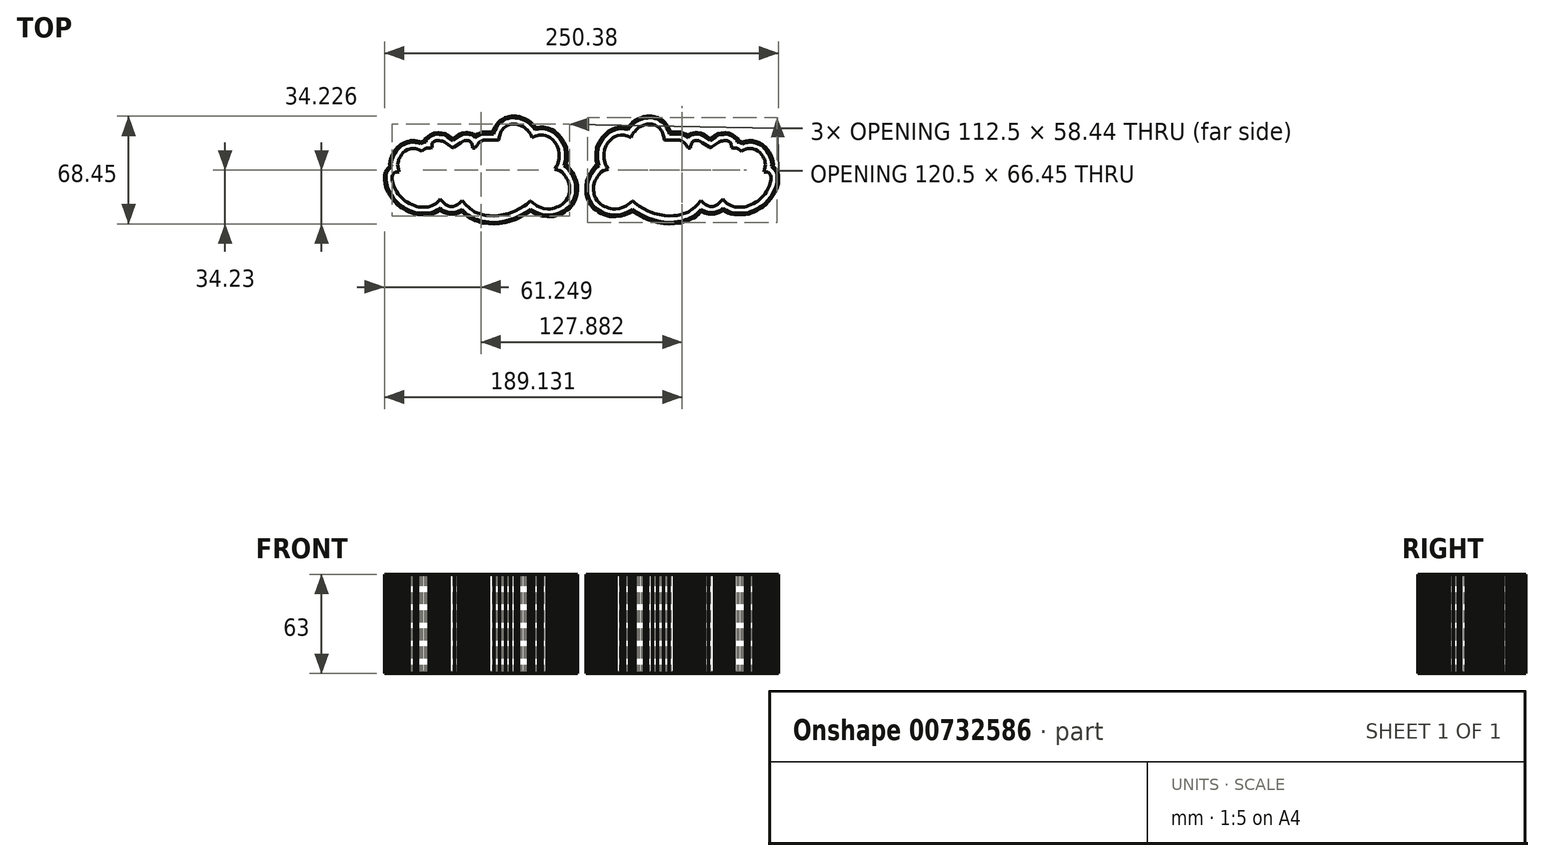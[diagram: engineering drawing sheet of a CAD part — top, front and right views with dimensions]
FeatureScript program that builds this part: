
annotation { "Feature Type Name" : "Feature", "Feature Type Description" : "" }
export const myFeature = defineFeature(function(context is Context, id is Id, definition is map)
    precondition{}
    {
        {
            var Q0;
            Q0=qCreatedBy(makeId("Top.planeOp"),FACE);
            var sketch = newSketch(context, id + "F0", { "sketchPlane" : qUnion([Q0])});
            skLineSegment(sketch, "E0", {"start": v(-23.19, 24.45) * mm, "end": v(-22.89, 24.98) * mm});
            skLineSegment(sketch, "E1", {"start": v(-22.89, 24.98) * mm, "end": v(-22.45, 25.83) * mm});
            skLineSegment(sketch, "E2", {"start": v(-22.45, 25.83) * mm, "end": v(-21.79, 26.88) * mm});
            skLineSegment(sketch, "E3", {"start": v(-21.79, 26.88) * mm, "end": v(-21.29, 27.75) * mm});
            skLineSegment(sketch, "E4", {"start": v(-21.29, 27.75) * mm, "end": v(-20.65, 28.52) * mm});
            skLineSegment(sketch, "E5", {"start": v(-20.65, 28.52) * mm, "end": v(-20.04, 29.22) * mm});
            skLineSegment(sketch, "E6", {"start": v(-20.04, 29.22) * mm, "end": v(-19.69, 29.6) * mm});
            skLineSegment(sketch, "E7", {"start": v(-19.69, 29.6) * mm, "end": v(-18.9, 30.34) * mm});
            skLineSegment(sketch, "E8", {"start": v(-18.9, 30.34) * mm, "end": v(-18.23, 30.85) * mm});
            skLineSegment(sketch, "E9", {"start": v(-18.23, 30.85) * mm, "end": v(-17.55, 31.28) * mm});
            skLineSegment(sketch, "E10", {"start": v(-17.55, 31.28) * mm, "end": v(-16.9, 31.62) * mm});
            skLineSegment(sketch, "E11", {"start": v(-16.9, 31.62) * mm, "end": v(-16.2, 31.87) * mm});
            skLineSegment(sketch, "E12", {"start": v(-16.2, 31.87) * mm, "end": v(-15.4, 32.17) * mm});
            skLineSegment(sketch, "E13", {"start": v(-15.4, 32.17) * mm, "end": v(-14.74, 32.39) * mm});
            skLineSegment(sketch, "E14", {"start": v(-14.74, 32.39) * mm, "end": v(-13.84, 32.5) * mm});
            skLineSegment(sketch, "E15", {"start": v(-13.84, 32.5) * mm, "end": v(-13.21, 32.57) * mm});
            skLineSegment(sketch, "E16", {"start": v(-13.21, 32.57) * mm, "end": v(-12.54, 32.64) * mm});
            skLineSegment(sketch, "E17", {"start": v(-12.54, 32.64) * mm, "end": v(-11.86, 32.64) * mm});
            skLineSegment(sketch, "E18", {"start": v(-11.86, 32.64) * mm, "end": v(-11.38, 32.52) * mm});
            skLineSegment(sketch, "E19", {"start": v(-11.38, 32.52) * mm, "end": v(-10.33, 32.21) * mm});
            skLineSegment(sketch, "E20", {"start": v(-10.33, 32.21) * mm, "end": v(-9.48, 32.02) * mm});
            skLineSegment(sketch, "E21", {"start": v(-9.48, 32.02) * mm, "end": v(-8.66, 31.5) * mm});
            skLineSegment(sketch, "E22", {"start": v(-8.66, 31.5) * mm, "end": v(-7.93, 31.02) * mm});
            skLineSegment(sketch, "E23", {"start": v(-7.93, 31.02) * mm, "end": v(-7.3, 30.45) * mm});
            skLineSegment(sketch, "E24", {"start": v(-7.3, 30.45) * mm, "end": v(-6.7, 29.75) * mm});
            skLineSegment(sketch, "E25", {"start": v(-6.7, 29.75) * mm, "end": v(-6.2, 29.04) * mm});
            skLineSegment(sketch, "E26", {"start": v(-6.2, 29.04) * mm, "end": v(-5.63, 27.97) * mm});
            skLineSegment(sketch, "E27", {"start": v(-5.63, 27.97) * mm, "end": v(-5.27, 26.99) * mm});
            skLineSegment(sketch, "E28", {"start": v(-5.27, 26.99) * mm, "end": v(-4.96, 25.96) * mm});
            skLineSegment(sketch, "E29", {"start": v(-4.96, 25.96) * mm, "end": v(-4.72, 25.15) * mm});
            skLineSegment(sketch, "E30", {"start": v(-4.72, 25.15) * mm, "end": v(-4.6, 24.61) * mm});
            skLineSegment(sketch, "E31", {"start": v(-4.6, 24.61) * mm, "end": v(-4.6, 23.66) * mm});
            skLineSegment(sketch, "E32", {"start": v(-4.6, 23.66) * mm, "end": v(-4.46, 23.42) * mm});
            skLineSegment(sketch, "E33", {"start": v(-4.46, 23.42) * mm, "end": v(-4.1, 23.02) * mm});
            skLineSegment(sketch, "E34", {"start": v(-4.1, 23.02) * mm, "end": v(-3.67, 22.68) * mm});
            skLineSegment(sketch, "E35", {"start": v(-3.67, 22.68) * mm, "end": v(-3.29, 22.5) * mm});
            skLineSegment(sketch, "E36", {"start": v(-3.29, 22.5) * mm, "end": v(-2.73, 22.4) * mm});
            skLineSegment(sketch, "E37", {"start": v(-2.73, 22.4) * mm, "end": v(-2.06, 22.4) * mm});
            skLineSegment(sketch, "E38", {"start": v(-2.06, 22.4) * mm, "end": v(6.4, 22.4) * mm});
            skLineSegment(sketch, "E39", {"start": v(6.4, 22.4) * mm, "end": v(6.78, 22.31) * mm});
            skLineSegment(sketch, "E40", {"start": v(6.78, 22.31) * mm, "end": v(7.37, 22.04) * mm});
            skLineSegment(sketch, "E41", {"start": v(7.37, 22.04) * mm, "end": v(8.12, 21.59) * mm});
            skLineSegment(sketch, "E42", {"start": v(8.12, 21.59) * mm, "end": v(8.57, 21.14) * mm});
            skLineSegment(sketch, "E43", {"start": v(8.57, 21.14) * mm, "end": v(9.34, 20.19) * mm});
            skLineSegment(sketch, "E44", {"start": v(9.34, 20.19) * mm, "end": v(9.63, 19.65) * mm});
            skLineSegment(sketch, "E45", {"start": v(9.63, 19.65) * mm, "end": v(10.05, 19.02) * mm});
            skLineSegment(sketch, "E46", {"start": v(10.05, 19.02) * mm, "end": v(10.48, 18.48) * mm});
            skLineSegment(sketch, "E47", {"start": v(10.48, 18.48) * mm, "end": v(10.93, 18.03) * mm});
            skLineSegment(sketch, "E48", {"start": v(10.93, 18.03) * mm, "end": v(11.34, 17.7) * mm});
            skLineSegment(sketch, "E49", {"start": v(11.34, 17.7) * mm, "end": v(11.6, 17.57) * mm});
            skLineSegment(sketch, "E50", {"start": v(11.6, 17.57) * mm, "end": v(11.99, 17.4) * mm});
            skLineSegment(sketch, "E51", {"start": v(11.99, 17.4) * mm, "end": v(13.78, 17.4) * mm});
            skLineSegment(sketch, "E52", {"start": v(13.78, 17.4) * mm, "end": v(14.24, 17.4) * mm});
            skLineSegment(sketch, "E53", {"start": v(14.24, 17.4) * mm, "end": v(14.42, 17.52) * mm});
            skLineSegment(sketch, "E54", {"start": v(14.42, 17.52) * mm, "end": v(14.71, 17.67) * mm});
            skLineSegment(sketch, "E55", {"start": v(14.71, 17.67) * mm, "end": v(14.85, 17.98) * mm});
            skLineSegment(sketch, "E56", {"start": v(14.85, 17.98) * mm, "end": v(14.98, 18.27) * mm});
            skLineSegment(sketch, "E57", {"start": v(14.98, 18.27) * mm, "end": v(15.1, 19.02) * mm});
            skLineSegment(sketch, "E58", {"start": v(15.1, 19.02) * mm, "end": v(15.19, 19.75) * mm});
            skLineSegment(sketch, "E59", {"start": v(15.19, 19.75) * mm, "end": v(15.37, 20.46) * mm});
            skLineSegment(sketch, "E60", {"start": v(15.37, 20.46) * mm, "end": v(15.51, 21.04) * mm});
            skLineSegment(sketch, "E61", {"start": v(15.51, 21.04) * mm, "end": v(15.68, 21.4) * mm});
            skLineSegment(sketch, "E62", {"start": v(15.68, 21.4) * mm, "end": v(15.93, 21.76) * mm});
            skLineSegment(sketch, "E63", {"start": v(15.93, 21.76) * mm, "end": v(16.28, 22.04) * mm});
            skLineSegment(sketch, "E64", {"start": v(16.28, 22.04) * mm, "end": v(16.59, 22.12) * mm});
            skLineSegment(sketch, "E65", {"start": v(16.59, 22.12) * mm, "end": v(17.21, 22.22) * mm});
            skLineSegment(sketch, "E66", {"start": v(17.21, 22.22) * mm, "end": v(17.73, 22.22) * mm});
            skLineSegment(sketch, "E67", {"start": v(17.73, 22.22) * mm, "end": v(18.51, 22.12) * mm});
            skLineSegment(sketch, "E68", {"start": v(18.51, 22.12) * mm, "end": v(19.1, 21.85) * mm});
            skLineSegment(sketch, "E69", {"start": v(19.1, 21.85) * mm, "end": v(20, 21.13) * mm});
            skLineSegment(sketch, "E70", {"start": v(20, 21.13) * mm, "end": v(24.79, 18.05) * mm});
            skLineSegment(sketch, "E71", {"start": v(24.79, 18.05) * mm, "end": v(25.26, 17.84) * mm});
            skLineSegment(sketch, "E72", {"start": v(25.26, 17.84) * mm, "end": v(25.52, 17.8) * mm});
            skLineSegment(sketch, "E73", {"start": v(25.52, 17.8) * mm, "end": v(26.08, 17.74) * mm});
            skLineSegment(sketch, "E74", {"start": v(26.08, 17.74) * mm, "end": v(26.62, 17.74) * mm});
            skLineSegment(sketch, "E75", {"start": v(26.62, 17.74) * mm, "end": v(27.51, 18.05) * mm});
            skLineSegment(sketch, "E76", {"start": v(27.51, 18.05) * mm, "end": v(32.34, 21.27) * mm});
            skLineSegment(sketch, "E77", {"start": v(32.34, 21.27) * mm, "end": v(33.33, 21.8) * mm});
            skLineSegment(sketch, "E78", {"start": v(33.33, 21.8) * mm, "end": v(34, 21.95) * mm});
            skLineSegment(sketch, "E79", {"start": v(34, 21.95) * mm, "end": v(35.03, 22.04) * mm});
            skLineSegment(sketch, "E80", {"start": v(35.03, 22.04) * mm, "end": v(35.66, 22.12) * mm});
            skLineSegment(sketch, "E81", {"start": v(35.66, 22.12) * mm, "end": v(36.26, 22.04) * mm});
            skLineSegment(sketch, "E82", {"start": v(36.26, 22.04) * mm, "end": v(37.14, 21.64) * mm});
            skLineSegment(sketch, "E83", {"start": v(37.14, 21.64) * mm, "end": v(37.79, 21.13) * mm});
            skLineSegment(sketch, "E84", {"start": v(37.79, 21.13) * mm, "end": v(37.86, 20.36) * mm});
            skLineSegment(sketch, "E85", {"start": v(37.86, 20.36) * mm, "end": v(37.93, 19.65) * mm});
            skLineSegment(sketch, "E86", {"start": v(37.93, 19.65) * mm, "end": v(38.02, 18.69) * mm});
            skLineSegment(sketch, "E87", {"start": v(38.02, 18.69) * mm, "end": v(38.44, 18.05) * mm});
            skLineSegment(sketch, "E88", {"start": v(38.44, 18.05) * mm, "end": v(38.7, 17.66) * mm});
            skLineSegment(sketch, "E89", {"start": v(38.7, 17.66) * mm, "end": v(39.43, 17.57) * mm});
            skLineSegment(sketch, "E90", {"start": v(39.43, 17.57) * mm, "end": v(40.57, 17.48) * mm});
            skLineSegment(sketch, "E91", {"start": v(40.57, 17.48) * mm, "end": v(41.83, 17.4) * mm});
            skLineSegment(sketch, "E92", {"start": v(41.83, 17.4) * mm, "end": v(42.56, 17.27) * mm});
            skLineSegment(sketch, "E93", {"start": v(42.56, 17.27) * mm, "end": v(43.28, 17) * mm});
            skLineSegment(sketch, "E94", {"start": v(43.28, 17) * mm, "end": v(44.02, 16.5) * mm});
            skLineSegment(sketch, "E95", {"start": v(44.02, 16.5) * mm, "end": v(44.44, 16.08) * mm});
            skLineSegment(sketch, "E96", {"start": v(44.44, 16.08) * mm, "end": v(44.78, 15.66) * mm});
            skLineSegment(sketch, "E97", {"start": v(44.78, 15.66) * mm, "end": v(45.06, 15.27) * mm});
            skLineSegment(sketch, "E98", {"start": v(45.06, 15.27) * mm, "end": v(45.22, 15.07) * mm});
            skLineSegment(sketch, "E99", {"start": v(45.22, 15.07) * mm, "end": v(45.45, 14.99) * mm});
            skLineSegment(sketch, "E100", {"start": v(45.45, 14.99) * mm, "end": v(45.83, 14.99) * mm});
            skLineSegment(sketch, "E101", {"start": v(45.83, 14.99) * mm, "end": v(46.12, 15.18) * mm});
            skLineSegment(sketch, "E102", {"start": v(46.12, 15.18) * mm, "end": v(46.84, 15.62) * mm});
            skLineSegment(sketch, "E103", {"start": v(46.84, 15.62) * mm, "end": v(47.97, 16.16) * mm});
            skLineSegment(sketch, "E104", {"start": v(47.97, 16.16) * mm, "end": v(49.46, 16.7) * mm});
            skLineSegment(sketch, "E105", {"start": v(49.46, 16.7) * mm, "end": v(50.25, 16.93) * mm});
            skLineSegment(sketch, "E106", {"start": v(50.25, 16.93) * mm, "end": v(50.8, 17.04) * mm});
            skLineSegment(sketch, "E107", {"start": v(52.56, 17.04) * mm, "end": v(53.3, 16.85) * mm});
            skLineSegment(sketch, "E108", {"start": v(52.56, 17.04) * mm, "end": v(52.1, 17.1) * mm});
            skLineSegment(sketch, "E109", {"start": v(52.1, 17.1) * mm, "end": v(51.65, 17.15) * mm});
            skLineSegment(sketch, "E110", {"start": v(51.65, 17.15) * mm, "end": v(51.34, 17.13) * mm});
            skLineSegment(sketch, "E111", {"start": v(51.34, 17.13) * mm, "end": v(50.8, 17.04) * mm});
            skLineSegment(sketch, "E112", {"start": v(53.3, 16.85) * mm, "end": v(54.34, 16.44) * mm});
            skLineSegment(sketch, "E113", {"start": v(54.34, 16.44) * mm, "end": v(55.66, 15.8) * mm});
            skLineSegment(sketch, "E114", {"start": v(55.66, 15.8) * mm, "end": v(56.62, 14.86) * mm});
            skLineSegment(sketch, "E115", {"start": v(56.62, 14.86) * mm, "end": v(57.37, 13.92) * mm});
            skLineSegment(sketch, "E116", {"start": v(57.37, 13.92) * mm, "end": v(58.22, 12.7) * mm});
            skLineSegment(sketch, "E117", {"start": v(58.22, 12.7) * mm, "end": v(58.75, 11.86) * mm});
            skLineSegment(sketch, "E118", {"start": v(58.75, 11.86) * mm, "end": v(59.07, 11.22) * mm});
            skLineSegment(sketch, "E119", {"start": v(59.07, 11.22) * mm, "end": v(59.32, 10.3) * mm});
            skLineSegment(sketch, "E120", {"start": v(59.32, 10.3) * mm, "end": v(59.5, 9.39) * mm});
            skLineSegment(sketch, "E121", {"start": v(59.5, 9.39) * mm, "end": v(59.66, 8.45) * mm});
            skLineSegment(sketch, "E122", {"start": v(59.66, 8.45) * mm, "end": v(59.5, 7.13) * mm});
            skLineSegment(sketch, "E123", {"start": v(59.5, 7.13) * mm, "end": v(59.3, 6.34) * mm});
            skLineSegment(sketch, "E124", {"start": v(59.3, 6.34) * mm, "end": v(58.97, 5.1) * mm});
            skLineSegment(sketch, "E125", {"start": v(58.97, 5.1) * mm, "end": v(58.74, 4.26) * mm});
            skLineSegment(sketch, "E126", {"start": v(58.74, 4.26) * mm, "end": v(58.65, 3.52) * mm});
            skLineSegment(sketch, "E127", {"start": v(58.65, 3.52) * mm, "end": v(58.6, 3.08) * mm});
            skLineSegment(sketch, "E128", {"start": v(58.6, 3.08) * mm, "end": v(58.7, 2.77) * mm});
            skLineSegment(sketch, "E129", {"start": v(58.7, 2.77) * mm, "end": v(59, 2.56) * mm});
            skLineSegment(sketch, "E130", {"start": v(59, 2.56) * mm, "end": v(59.68, 2.22) * mm});
            skLineSegment(sketch, "E131", {"start": v(59.68, 2.22) * mm, "end": v(60.73, 2.22) * mm});
            skLineSegment(sketch, "E132", {"start": v(60.73, 2.22) * mm, "end": v(61.38, 2.22) * mm});
            skLineSegment(sketch, "E133", {"start": v(61.38, 2.22) * mm, "end": v(62.24, 2.11) * mm});
            skLineSegment(sketch, "E134", {"start": v(62.24, 2.11) * mm, "end": v(62.62, 1.76) * mm});
            skLineSegment(sketch, "E135", {"start": v(62.62, 1.76) * mm, "end": v(62.98, 1.18) * mm});
            skLineSegment(sketch, "E136", {"start": v(62.98, 1.18) * mm, "end": v(63.1, 0.71) * mm});
            skLineSegment(sketch, "E137", {"start": v(63.1, 0.71) * mm, "end": v(63.1, -1.46) * mm});
            skLineSegment(sketch, "E138", {"start": v(63.1, -1.46) * mm, "end": v(62.98, -2.25) * mm});
            skLineSegment(sketch, "E139", {"start": v(62.98, -2.25) * mm, "end": v(62.32, -4.45) * mm});
            skLineSegment(sketch, "E140", {"start": v(62.32, -4.45) * mm, "end": v(61.45, -6.3) * mm});
            skLineSegment(sketch, "E141", {"start": v(61.45, -6.3) * mm, "end": v(60.5, -8.05) * mm});
            skLineSegment(sketch, "E142", {"start": v(60.5, -8.05) * mm, "end": v(59.65, -9.33) * mm});
            skLineSegment(sketch, "E143", {"start": v(59.65, -9.33) * mm, "end": v(58.43, -10.74) * mm});
            skLineSegment(sketch, "E144", {"start": v(58.43, -10.74) * mm, "end": v(57.04, -12.18) * mm});
            skLineSegment(sketch, "E145", {"start": v(57.04, -12.18) * mm, "end": v(55.54, -13.41) * mm});
            skLineSegment(sketch, "E146", {"start": v(55.54, -13.41) * mm, "end": v(54.48, -14) * mm});
            skLineSegment(sketch, "E147", {"start": v(54.48, -14) * mm, "end": v(52.93, -15.02) * mm});
            skLineSegment(sketch, "E148", {"start": v(52.93, -15.02) * mm, "end": v(51.54, -15.59) * mm});
            skLineSegment(sketch, "E149", {"start": v(51.54, -15.59) * mm, "end": v(49.77, -16.27) * mm});
            skLineSegment(sketch, "E150", {"start": v(49.77, -16.27) * mm, "end": v(48.65, -16.7) * mm});
            skLineSegment(sketch, "E151", {"start": v(48.65, -16.7) * mm, "end": v(47.64, -16.95) * mm});
            skLineSegment(sketch, "E152", {"start": v(47.64, -16.95) * mm, "end": v(45.57, -16.95) * mm});
            skLineSegment(sketch, "E153", {"start": v(45.57, -16.95) * mm, "end": v(44.46, -16.95) * mm});
            skLineSegment(sketch, "E154", {"start": v(44.46, -16.95) * mm, "end": v(42.04, -16.95) * mm});
            skLineSegment(sketch, "E155", {"start": v(42.04, -16.95) * mm, "end": v(41.33, -16.76) * mm});
            skLineSegment(sketch, "E156", {"start": v(41.33, -16.76) * mm, "end": v(39.87, -16.27) * mm});
            skLineSegment(sketch, "E157", {"start": v(39.87, -16.27) * mm, "end": v(38.74, -15.7) * mm});
            skLineSegment(sketch, "E158", {"start": v(38.74, -15.7) * mm, "end": v(37.6, -15.02) * mm});
            skLineSegment(sketch, "E159", {"start": v(37.6, -15.02) * mm, "end": v(36.86, -14.4) * mm});
            skLineSegment(sketch, "E160", {"start": v(36.86, -14.4) * mm, "end": v(36.02, -13.56) * mm});
            skLineSegment(sketch, "E161", {"start": v(36.02, -13.56) * mm, "end": v(35.63, -12.92) * mm});
            skLineSegment(sketch, "E162", {"start": v(35.63, -12.92) * mm, "end": v(35.3, -12.62) * mm});
            skLineSegment(sketch, "E163", {"start": v(35.3, -12.62) * mm, "end": v(34.75, -12.28) * mm});
            skLineSegment(sketch, "E164", {"start": v(34.75, -12.28) * mm, "end": v(34.2, -12.16) * mm});
            skLineSegment(sketch, "E165", {"start": v(34.2, -12.16) * mm, "end": v(33.87, -12.16) * mm});
            skLineSegment(sketch, "E166", {"start": v(33.87, -12.16) * mm, "end": v(33.46, -12.28) * mm});
            skLineSegment(sketch, "E167", {"start": v(33.46, -12.28) * mm, "end": v(32.88, -12.71) * mm});
            skLineSegment(sketch, "E168", {"start": v(32.88, -12.71) * mm, "end": v(32.2, -13.33) * mm});
            skLineSegment(sketch, "E169", {"start": v(32.2, -13.33) * mm, "end": v(31.66, -13.97) * mm});
            skLineSegment(sketch, "E170", {"start": v(31.66, -13.97) * mm, "end": v(31.09, -14.62) * mm});
            skLineSegment(sketch, "E171", {"start": v(31.09, -14.62) * mm, "end": v(30.4, -15.25) * mm});
            skLineSegment(sketch, "E172", {"start": v(30.4, -15.25) * mm, "end": v(29.83, -15.78) * mm});
            skLineSegment(sketch, "E173", {"start": v(29.83, -15.78) * mm, "end": v(28.97, -16.17) * mm});
            skLineSegment(sketch, "E174", {"start": v(28.97, -16.17) * mm, "end": v(28.35, -16.47) * mm});
            skLineSegment(sketch, "E175", {"start": v(28.35, -16.47) * mm, "end": v(27.64, -16.7) * mm});
            skLineSegment(sketch, "E176", {"start": v(27.64, -16.7) * mm, "end": v(26.22, -16.7) * mm});
            skLineSegment(sketch, "E177", {"start": v(26.22, -16.7) * mm, "end": v(24.96, -16.26) * mm});
            skLineSegment(sketch, "E178", {"start": v(24.96, -16.26) * mm, "end": v(23.9, -15.83) * mm});
            skLineSegment(sketch, "E179", {"start": v(23.9, -15.83) * mm, "end": v(22.93, -15.02) * mm});
            skLineSegment(sketch, "E180", {"start": v(22.93, -15.02) * mm, "end": v(22, -14.1) * mm});
            skLineSegment(sketch, "E181", {"start": v(22, -14.1) * mm, "end": v(21.4, -13.46) * mm});
            skLineSegment(sketch, "E182", {"start": v(21.4, -13.46) * mm, "end": v(20.93, -12.95) * mm});
            skLineSegment(sketch, "E183", {"start": v(20.93, -12.95) * mm, "end": v(20.55, -12.71) * mm});
            skLineSegment(sketch, "E184", {"start": v(20.55, -12.71) * mm, "end": v(20.2, -12.6) * mm});
            skLineSegment(sketch, "E185", {"start": v(20.2, -12.6) * mm, "end": v(19.88, -12.6) * mm});
            skLineSegment(sketch, "E186", {"start": v(19.88, -12.6) * mm, "end": v(19.69, -12.71) * mm});
            skLineSegment(sketch, "E187", {"start": v(19.69, -12.71) * mm, "end": v(19.32, -12.93) * mm});
            skLineSegment(sketch, "E188", {"start": v(19.32, -12.93) * mm, "end": v(19.06, -13.21) * mm});
            skLineSegment(sketch, "E189", {"start": v(19.06, -13.21) * mm, "end": v(18.73, -13.73) * mm});
            skLineSegment(sketch, "E190", {"start": v(18.73, -13.73) * mm, "end": v(18.12, -14.51) * mm});
            skLineSegment(sketch, "E191", {"start": v(18.12, -14.51) * mm, "end": v(17.32, -15.57) * mm});
            skLineSegment(sketch, "E192", {"start": v(17.32, -15.57) * mm, "end": v(16.25, -16.6) * mm});
            skLineSegment(sketch, "E193", {"start": v(16.25, -16.6) * mm, "end": v(15.3, -17.51) * mm});
            skLineSegment(sketch, "E194", {"start": v(15.3, -17.51) * mm, "end": v(14.34, -18.4) * mm});
            skLineSegment(sketch, "E195", {"start": v(14.34, -18.4) * mm, "end": v(13.2, -19.26) * mm});
            skLineSegment(sketch, "E196", {"start": v(13.2, -19.26) * mm, "end": v(12.21, -19.9) * mm});
            skLineSegment(sketch, "E197", {"start": v(12.21, -19.9) * mm, "end": v(11.5, -20.3) * mm});
            skLineSegment(sketch, "E198", {"start": v(11.5, -20.3) * mm, "end": v(10.72, -20.68) * mm});
            skLineSegment(sketch, "E199", {"start": v(10.72, -20.68) * mm, "end": v(10.03, -20.96) * mm});
            skLineSegment(sketch, "E200", {"start": v(10.03, -20.96) * mm, "end": v(8.74, -21.44) * mm});
            skLineSegment(sketch, "E201", {"start": v(8.74, -21.44) * mm, "end": v(7.25, -21.93) * mm});
            skLineSegment(sketch, "E202", {"start": v(7.25, -21.93) * mm, "end": v(6.02, -22.25) * mm});
            skLineSegment(sketch, "E203", {"start": v(6.02, -22.25) * mm, "end": v(4.78, -22.43) * mm});
            skLineSegment(sketch, "E204", {"start": v(4.78, -22.43) * mm, "end": v(2.83, -22.61) * mm});
            skLineSegment(sketch, "E205", {"start": v(2.83, -22.61) * mm, "end": v(0, -22.8) * mm});
            skLineSegment(sketch, "E206", {"start": v(0, -22.8) * mm, "end": v(-2.68, -22.61) * mm});
            skLineSegment(sketch, "E207", {"start": v(-2.68, -22.61) * mm, "end": v(-5.85, -22.02) * mm});
            skLineSegment(sketch, "E208", {"start": v(-5.85, -22.02) * mm, "end": v(-8.79, -21.25) * mm});
            skLineSegment(sketch, "E209", {"start": v(-8.79, -21.25) * mm, "end": v(-11.22, -20.48) * mm});
            skLineSegment(sketch, "E210", {"start": v(-11.22, -20.48) * mm, "end": v(-12.72, -19.75) * mm});
            skLineSegment(sketch, "E211", {"start": v(-12.72, -19.75) * mm, "end": v(-15.07, -18.48) * mm});
            skLineSegment(sketch, "E212", {"start": v(-15.07, -18.48) * mm, "end": v(-16.87, -17.51) * mm});
            skLineSegment(sketch, "E213", {"start": v(-16.87, -17.51) * mm, "end": v(-18.26, -16.77) * mm});
            skLineSegment(sketch, "E214", {"start": v(-18.26, -16.77) * mm, "end": v(-19.59, -15.76) * mm});
            skLineSegment(sketch, "E215", {"start": v(-19.59, -15.76) * mm, "end": v(-20.68, -14.88) * mm});
            skLineSegment(sketch, "E216", {"start": v(-20.68, -14.88) * mm, "end": v(-21.63, -14.01) * mm});
            skLineSegment(sketch, "E217", {"start": v(-21.63, -14.01) * mm, "end": v(-22.15, -13.63) * mm});
            skLineSegment(sketch, "E218", {"start": v(-22.15, -13.63) * mm, "end": v(-22.7, -13.28) * mm});
            skLineSegment(sketch, "E219", {"start": v(-22.7, -13.28) * mm, "end": v(-22.94, -13.2) * mm});
            skLineSegment(sketch, "E220", {"start": v(-22.94, -13.2) * mm, "end": v(-23.33, -13.11) * mm});
            skLineSegment(sketch, "E221", {"start": v(-23.33, -13.11) * mm, "end": v(-23.72, -13.11) * mm});
            skLineSegment(sketch, "E222", {"start": v(-23.72, -13.11) * mm, "end": v(-24.3, -13.47) * mm});
            skLineSegment(sketch, "E223", {"start": v(-24.3, -13.47) * mm, "end": v(-25.14, -14.38) * mm});
            skLineSegment(sketch, "E224", {"start": v(-25.14, -14.38) * mm, "end": v(-25.78, -14.86) * mm});
            skLineSegment(sketch, "E225", {"start": v(-25.78, -14.86) * mm, "end": v(-26.58, -15.53) * mm});
            skLineSegment(sketch, "E226", {"start": v(-26.58, -15.53) * mm, "end": v(-27.49, -16.2) * mm});
            skLineSegment(sketch, "E227", {"start": v(-27.49, -16.2) * mm, "end": v(-28.16, -16.56) * mm});
            skLineSegment(sketch, "E228", {"start": v(-28.16, -16.56) * mm, "end": v(-29.08, -16.97) * mm});
            skLineSegment(sketch, "E229", {"start": v(-29.08, -16.97) * mm, "end": v(-30.46, -17.58) * mm});
            skLineSegment(sketch, "E230", {"start": v(-30.46, -17.58) * mm, "end": v(-31.71, -17.94) * mm});
            skLineSegment(sketch, "E231", {"start": v(-31.71, -17.94) * mm, "end": v(-32.92, -18.08) * mm});
            skLineSegment(sketch, "E232", {"start": v(-32.92, -18.08) * mm, "end": v(-34.12, -18.21) * mm});
            skLineSegment(sketch, "E233", {"start": v(-34.12, -18.21) * mm, "end": v(-35.65, -18.21) * mm});
            skLineSegment(sketch, "E234", {"start": v(-35.65, -18.21) * mm, "end": v(-36.89, -18.08) * mm});
            skLineSegment(sketch, "E235", {"start": v(-36.89, -18.08) * mm, "end": v(-37.9, -17.86) * mm});
            skLineSegment(sketch, "E236", {"start": v(-37.9, -17.86) * mm, "end": v(-39.24, -17.35) * mm});
            skLineSegment(sketch, "E237", {"start": v(-39.24, -17.35) * mm, "end": v(-40.18, -16.9) * mm});
            skLineSegment(sketch, "E238", {"start": v(-40.18, -16.9) * mm, "end": v(-41.32, -16.29) * mm});
            skLineSegment(sketch, "E239", {"start": v(-41.32, -16.29) * mm, "end": v(-42.58, -15.32) * mm});
            skLineSegment(sketch, "E240", {"start": v(-42.58, -15.32) * mm, "end": v(-43.5, -14.7) * mm});
            skLineSegment(sketch, "E241", {"start": v(-43.5, -14.7) * mm, "end": v(-44.48, -13.53) * mm});
            skLineSegment(sketch, "E242", {"start": v(-44.48, -13.53) * mm, "end": v(-45.37, -12.03) * mm});
            skLineSegment(sketch, "E243", {"start": v(-45.37, -12.03) * mm, "end": v(-45.81, -11.1) * mm});
            skLineSegment(sketch, "E244", {"start": v(-45.81, -11.1) * mm, "end": v(-46.12, -10.04) * mm});
            skLineSegment(sketch, "E245", {"start": v(-46.12, -10.04) * mm, "end": v(-46.31, -9.23) * mm});
            skLineSegment(sketch, "E246", {"start": v(-46.31, -9.23) * mm, "end": v(-46.4, -7.94) * mm});
            skLineSegment(sketch, "E247", {"start": v(-46.4, -7.94) * mm, "end": v(-46.4, -5.56) * mm});
            skLineSegment(sketch, "E248", {"start": v(-46.4, -5.56) * mm, "end": v(-46.12, -3.98) * mm});
            skLineSegment(sketch, "E249", {"start": v(-46.12, -3.98) * mm, "end": v(-45.56, -2.54) * mm});
            skLineSegment(sketch, "E250", {"start": v(-45.56, -2.54) * mm, "end": v(-44.88, -1.23) * mm});
            skLineSegment(sketch, "E251", {"start": v(-44.88, -1.23) * mm, "end": v(-44.27, 0) * mm});
            skLineSegment(sketch, "E252", {"start": v(-44.27, 0) * mm, "end": v(-43.38, 1.26) * mm});
            skLineSegment(sketch, "E253", {"start": v(-43.38, 1.26) * mm, "end": v(-42.37, 2.54) * mm});
            skLineSegment(sketch, "E254", {"start": v(-42.37, 2.54) * mm, "end": v(-41.18, 3.16) * mm});
            skLineSegment(sketch, "E255", {"start": v(-41.18, 3.16) * mm, "end": v(-40.15, 3.46) * mm});
            skLineSegment(sketch, "E256", {"start": v(-40.15, 3.46) * mm, "end": v(-38.85, 3.84) * mm});
            skLineSegment(sketch, "E257", {"start": v(-38.85, 3.84) * mm, "end": v(-37.75, 4.06) * mm});
            skLineSegment(sketch, "E258", {"start": v(-37.75, 4.06) * mm, "end": v(-37.12, 4.24) * mm});
            skLineSegment(sketch, "E259", {"start": v(-37.12, 4.24) * mm, "end": v(-36.89, 4.44) * mm});
            skLineSegment(sketch, "E260", {"start": v(-36.89, 4.44) * mm, "end": v(-36.75, 4.68) * mm});
            skLineSegment(sketch, "E261", {"start": v(-36.75, 4.68) * mm, "end": v(-36.8, 4.84) * mm});
            skLineSegment(sketch, "E262", {"start": v(-36.8, 4.84) * mm, "end": v(-36.8, 5.61) * mm});
            skLineSegment(sketch, "E263", {"start": v(-36.8, 5.61) * mm, "end": v(-37.6, 6.57) * mm});
            skLineSegment(sketch, "E264", {"start": v(-37.6, 6.57) * mm, "end": v(-38.36, 7.9) * mm});
            skLineSegment(sketch, "E265", {"start": v(-38.36, 7.9) * mm, "end": v(-39.04, 9.1) * mm});
            skLineSegment(sketch, "E266", {"start": v(-39.04, 9.1) * mm, "end": v(-39.38, 10.27) * mm});
            skLineSegment(sketch, "E267", {"start": v(-39.38, 10.27) * mm, "end": v(-39.87, 11.94) * mm});
            skLineSegment(sketch, "E268", {"start": v(-39.87, 11.94) * mm, "end": v(-39.87, 13.44) * mm});
            skLineSegment(sketch, "E269", {"start": v(-39.87, 13.44) * mm, "end": v(-39.87, 15.15) * mm});
            skLineSegment(sketch, "E270", {"start": v(-39.87, 15.15) * mm, "end": v(-39.61, 17.48) * mm});
            skLineSegment(sketch, "E271", {"start": v(-39.61, 17.48) * mm, "end": v(-38.72, 19.62) * mm});
            skLineSegment(sketch, "E272", {"start": v(-38.72, 19.62) * mm, "end": v(-37.46, 21.52) * mm});
            skLineSegment(sketch, "E273", {"start": v(-37.46, 21.52) * mm, "end": v(-35.97, 23.24) * mm});
            skLineSegment(sketch, "E274", {"start": v(-35.97, 23.24) * mm, "end": v(-34.9, 24.13) * mm});
            skLineSegment(sketch, "E275", {"start": v(-34.9, 24.13) * mm, "end": v(-33.76, 24.76) * mm});
            skLineSegment(sketch, "E276", {"start": v(-33.76, 24.76) * mm, "end": v(-32.34, 25.42) * mm});
            skLineSegment(sketch, "E277", {"start": v(-32.34, 25.42) * mm, "end": v(-30.87, 25.66) * mm});
            skLineSegment(sketch, "E278", {"start": v(-30.87, 25.66) * mm, "end": v(-29.82, 25.66) * mm});
            skLineSegment(sketch, "E279", {"start": v(-29.82, 25.66) * mm, "end": v(-28.75, 25.53) * mm});
            skLineSegment(sketch, "E280", {"start": v(-28.75, 25.53) * mm, "end": v(-27.78, 25.4) * mm});
            skLineSegment(sketch, "E281", {"start": v(-27.78, 25.4) * mm, "end": v(-26.78, 25.2) * mm});
            skLineSegment(sketch, "E282", {"start": v(-26.78, 25.2) * mm, "end": v(-25.47, 24.64) * mm});
            skLineSegment(sketch, "E283", {"start": v(-25.47, 24.64) * mm, "end": v(-24.9, 24.25) * mm});
            skLineSegment(sketch, "E284", {"start": v(-24.9, 24.25) * mm, "end": v(-24.44, 24) * mm});
            skLineSegment(sketch, "E285", {"start": v(-24.44, 24) * mm, "end": v(-24.2, 23.9) * mm});
            skLineSegment(sketch, "E286", {"start": v(-24.2, 23.9) * mm, "end": v(-23.83, 23.96) * mm});
            skLineSegment(sketch, "E287", {"start": v(-23.19, 24.45) * mm, "end": v(-23.41, 24.17) * mm});
            skLineSegment(sketch, "E288", {"start": v(-23.41, 24.17) * mm, "end": v(-23.83, 23.96) * mm});
            skSolve(sketch);
        }
        {
            var Q0;
            Q0=qCreatedBy(makeId("Top.planeOp"),FACE);
            var sketch = newSketch(context, id + "F1", { "sketchPlane" : qUnion([Q0])});
            skLineSegment(sketch, "E289.0", {"start": v(-24.24, 25.62) * mm, "end": v(-24.75, 25.97) * mm});
            skLineSegment(sketch, "E289.1", {"start": v(-23.76, 26.58) * mm, "end": v(-24.24, 25.62) * mm});
            skLineSegment(sketch, "E289.2", {"start": v(-23.07, 27.66) * mm, "end": v(-23.76, 26.58) * mm});
            skLineSegment(sketch, "E289.3", {"start": v(-22.52, 28.6) * mm, "end": v(-23.07, 27.66) * mm});
            skLineSegment(sketch, "E289.4", {"start": v(-21.8, 29.5) * mm, "end": v(-22.52, 28.6) * mm});
            skLineSegment(sketch, "E289.5", {"start": v(-21.15, 30.22) * mm, "end": v(-21.8, 29.5) * mm});
            skLineSegment(sketch, "E289.6", {"start": v(-20.76, 30.65) * mm, "end": v(-21.15, 30.22) * mm});
            skLineSegment(sketch, "E289.7", {"start": v(-19.87, 31.5) * mm, "end": v(-20.76, 30.65) * mm});
            skLineSegment(sketch, "E289.8", {"start": v(-19.08, 32.08) * mm, "end": v(-19.87, 31.5) * mm});
            skLineSegment(sketch, "E289.9", {"start": v(-18.3, 32.58) * mm, "end": v(-19.08, 32.08) * mm});
            skLineSegment(sketch, "E289.10", {"start": v(-17.5, 33) * mm, "end": v(-18.3, 32.58) * mm});
            skLineSegment(sketch, "E289.11", {"start": v(-16.72, 33.28) * mm, "end": v(-17.5, 33) * mm});
            skLineSegment(sketch, "E289.12", {"start": v(-15.89, 33.59) * mm, "end": v(-16.72, 33.28) * mm});
            skLineSegment(sketch, "E289.13", {"start": v(-15.07, 33.86) * mm, "end": v(-15.89, 33.59) * mm});
            skLineSegment(sketch, "E289.14", {"start": v(-14.02, 33.99) * mm, "end": v(-15.07, 33.86) * mm});
            skLineSegment(sketch, "E289.15", {"start": v(-13.37, 34.06) * mm, "end": v(-14.02, 33.99) * mm});
            skLineSegment(sketch, "E289.16", {"start": v(-12.61, 34.14) * mm, "end": v(-13.37, 34.06) * mm});
            skLineSegment(sketch, "E289.17", {"start": v(-11.68, 34.14) * mm, "end": v(-12.61, 34.14) * mm});
            skLineSegment(sketch, "E289.18", {"start": v(-10.99, 33.97) * mm, "end": v(-11.68, 34.14) * mm});
            skLineSegment(sketch, "E289.19", {"start": v(-9.95, 33.67) * mm, "end": v(-10.99, 33.97) * mm});
            skLineSegment(sketch, "E289.20", {"start": v(-8.89, 33.42) * mm, "end": v(-9.95, 33.67) * mm});
            skLineSegment(sketch, "E289.21", {"start": v(-7.86, 32.76) * mm, "end": v(-8.89, 33.42) * mm});
            skLineSegment(sketch, "E289.22", {"start": v(-7.01, 32.22) * mm, "end": v(-7.86, 32.76) * mm});
            skLineSegment(sketch, "E289.23", {"start": v(-6.22, 31.5) * mm, "end": v(-7.01, 32.22) * mm});
            skLineSegment(sketch, "E289.24", {"start": v(-5.51, 30.67) * mm, "end": v(-6.22, 31.5) * mm});
            skLineSegment(sketch, "E289.25", {"start": v(-4.92, 29.83) * mm, "end": v(-5.51, 30.67) * mm});
            skLineSegment(sketch, "E289.26", {"start": v(-4.26, 28.58) * mm, "end": v(-4.92, 29.83) * mm});
            skLineSegment(sketch, "E289.27", {"start": v(-3.85, 27.47) * mm, "end": v(-4.26, 28.58) * mm});
            skLineSegment(sketch, "E289.28", {"start": v(-3.52, 26.38) * mm, "end": v(-3.85, 27.47) * mm});
            skLineSegment(sketch, "E289.29", {"start": v(-3.28, 25.54) * mm, "end": v(-3.52, 26.38) * mm});
            skLineSegment(sketch, "E289.30", {"start": v(-3.1, 24.8) * mm, "end": v(-3.28, 25.54) * mm});
            skLineSegment(sketch, "E289.31", {"start": v(-3.1, 24.14) * mm, "end": v(-3.1, 24.8) * mm});
            skLineSegment(sketch, "E289.32", {"start": v(-2.84, 23.94) * mm, "end": v(-3.1, 24.14) * mm});
            skLineSegment(sketch, "E289.33", {"start": v(-2.6, 23.9) * mm, "end": v(-2.84, 23.94) * mm});
            skLineSegment(sketch, "E289.34", {"start": v(-1.7, 23.9) * mm, "end": v(-2.6, 23.9) * mm});
            skLineSegment(sketch, "E289.35", {"start": v(6.59, 23.9) * mm, "end": v(-1.7, 23.9) * mm});
            skLineSegment(sketch, "E289.36", {"start": v(7.28, 23.73) * mm, "end": v(6.59, 23.9) * mm});
            skLineSegment(sketch, "E289.37", {"start": v(8.07, 23.37) * mm, "end": v(7.28, 23.73) * mm});
            skLineSegment(sketch, "E289.38", {"start": v(9.06, 22.78) * mm, "end": v(8.07, 23.37) * mm});
            skLineSegment(sketch, "E289.39", {"start": v(32.8, -14.95) * mm, "end": v(33.29, -14.38) * mm});
            skLineSegment(sketch, "E289.40", {"start": v(32.16, -15.68) * mm, "end": v(32.8, -14.95) * mm});
            skLineSegment(sketch, "E289.43", {"start": v(29.6, -17.53) * mm, "end": v(30.67, -17.04) * mm});
            skLineSegment(sketch, "E289.44", {"start": v(28.91, -17.86) * mm, "end": v(29.6, -17.53) * mm});
            skLineSegment(sketch, "E289.45", {"start": v(27.88, -18.2) * mm, "end": v(28.91, -17.86) * mm});
            skLineSegment(sketch, "E289.46", {"start": v(25.96, -18.2) * mm, "end": v(27.88, -18.2) * mm});
            skLineSegment(sketch, "E289.47", {"start": v(24.42, -17.66) * mm, "end": v(25.96, -18.2) * mm});
            skLineSegment(sketch, "E289.48", {"start": v(23.12, -17.13) * mm, "end": v(24.42, -17.66) * mm});
            skLineSegment(sketch, "E289.49", {"start": v(21.93, -16.14) * mm, "end": v(23.12, -17.13) * mm});
            skLineSegment(sketch, "E289.50", {"start": v(20.91, -15.14) * mm, "end": v(21.93, -16.14) * mm});
            skLineSegment(sketch, "E289.51", {"start": v(20.17, -14.33) * mm, "end": v(20.91, -15.14) * mm});
            skLineSegment(sketch, "E289.52", {"start": v(19.31, -15.43) * mm, "end": v(20.17, -14.33) * mm});
            skLineSegment(sketch, "E289.53", {"start": v(18.45, -16.57) * mm, "end": v(19.31, -15.43) * mm});
            skLineSegment(sketch, "E289.54", {"start": v(17.29, -17.69) * mm, "end": v(18.45, -16.57) * mm});
            skLineSegment(sketch, "E289.55", {"start": v(16.33, -18.6) * mm, "end": v(17.29, -17.69) * mm});
            skLineSegment(sketch, "E289.56", {"start": v(15.3, -19.55) * mm, "end": v(16.33, -18.6) * mm});
            skLineSegment(sketch, "E289.57", {"start": v(14.06, -20.5) * mm, "end": v(15.3, -19.55) * mm});
            skLineSegment(sketch, "E289.58", {"start": v(12.98, -21.19) * mm, "end": v(14.06, -20.5) * mm});
            skLineSegment(sketch, "E289.59", {"start": v(12.2, -21.62) * mm, "end": v(12.98, -21.19) * mm});
            skLineSegment(sketch, "E289.60", {"start": v(11.33, -22.05) * mm, "end": v(12.2, -21.62) * mm});
            skLineSegment(sketch, "E289.61", {"start": v(10.57, -22.36) * mm, "end": v(11.33, -22.05) * mm});
            skLineSegment(sketch, "E289.62", {"start": v(9.23, -22.86) * mm, "end": v(10.57, -22.36) * mm});
            skLineSegment(sketch, "E289.63", {"start": v(7.67, -23.37) * mm, "end": v(9.23, -22.86) * mm});
            skLineSegment(sketch, "E289.64", {"start": v(6.31, -23.73) * mm, "end": v(7.67, -23.37) * mm});
            skLineSegment(sketch, "E289.65", {"start": v(4.95, -23.92) * mm, "end": v(6.31, -23.73) * mm});
            skLineSegment(sketch, "E289.66", {"start": v(2.95, -24.1) * mm, "end": v(4.95, -23.92) * mm});
            skLineSegment(sketch, "E289.67", {"start": v(0, -24.3) * mm, "end": v(2.95, -24.1) * mm});
            skLineSegment(sketch, "E289.68", {"start": v(-2.87, -24.1) * mm, "end": v(0, -24.3) * mm});
            skLineSegment(sketch, "E289.69", {"start": v(-6.17, -23.48) * mm, "end": v(-2.87, -24.1) * mm});
            skLineSegment(sketch, "E289.70", {"start": v(-9.2, -22.7) * mm, "end": v(-6.17, -23.48) * mm});
            skLineSegment(sketch, "E289.71", {"start": v(-11.77, -21.88) * mm, "end": v(-9.2, -22.7) * mm});
            skLineSegment(sketch, "E289.72", {"start": v(-13.4, -21.08) * mm, "end": v(-11.77, -21.88) * mm});
            skLineSegment(sketch, "E289.73", {"start": v(-15.08, -20.18) * mm, "end": v(-13.4, -21.08) * mm});
            skLineSegment(sketch, "E289.74", {"start": v(-16.56, -19.38) * mm, "end": v(-15.08, -20.18) * mm});
            skLineSegment(sketch, "E289.75", {"start": v(-19.08, -18.03) * mm, "end": v(-16.56, -19.38) * mm});
            skLineSegment(sketch, "E289.76", {"start": v(-20.51, -16.94) * mm, "end": v(-19.08, -18.03) * mm});
            skLineSegment(sketch, "E289.77", {"start": v(-21.65, -16.02) * mm, "end": v(-20.51, -16.94) * mm});
            skLineSegment(sketch, "E289.78", {"start": v(-22.58, -15.17) * mm, "end": v(-21.65, -16.02) * mm});
            skLineSegment(sketch, "E289.79", {"start": v(-23, -14.87) * mm, "end": v(-22.58, -15.17) * mm});
            skLineSegment(sketch, "E289.80", {"start": v(-23.34, -14.65) * mm, "end": v(-23, -14.87) * mm});
            skLineSegment(sketch, "E289.81", {"start": v(-24.13, -15.5) * mm, "end": v(-23.34, -14.65) * mm});
            skLineSegment(sketch, "E289.82", {"start": v(-24.85, -16.04) * mm, "end": v(-24.13, -15.5) * mm});
            skLineSegment(sketch, "E289.83", {"start": v(-25.65, -16.7) * mm, "end": v(-24.85, -16.04) * mm});
            skLineSegment(sketch, "E289.84", {"start": v(-26.68, -17.46) * mm, "end": v(-25.65, -16.7) * mm});
            skLineSegment(sketch, "E289.85", {"start": v(-27.5, -17.9) * mm, "end": v(-26.68, -17.46) * mm});
            skLineSegment(sketch, "E289.88", {"start": v(-31.42, -19.42) * mm, "end": v(-29.94, -18.99) * mm});
            skLineSegment(sketch, "E289.91", {"start": v(-38.66, 5.4) * mm, "end": v(-39.2, 5.3) * mm});
            skLineSegment(sketch, "E289.92", {"start": v(-39.66, 7.16) * mm, "end": v(-38.66, 5.4) * mm});
            skLineSegment(sketch, "E289.93", {"start": v(-40.43, 8.52) * mm, "end": v(-39.66, 7.16) * mm});
            skLineSegment(sketch, "E289.98", {"start": v(-41.08, 17.86) * mm, "end": v(-41.37, 15.23) * mm});
            skLineSegment(sketch, "E289.99", {"start": v(-40.05, 20.32) * mm, "end": v(-41.08, 17.86) * mm});
            skLineSegment(sketch, "E289.100", {"start": v(-38.66, 22.43) * mm, "end": v(-40.05, 20.32) * mm});
            skLineSegment(sketch, "E289.101", {"start": v(-28.56, 27.02) * mm, "end": v(-29.73, 27.16) * mm});
            skLineSegment(sketch, "E289.102", {"start": v(-27.53, 26.88) * mm, "end": v(-28.56, 27.02) * mm});
            skLineSegment(sketch, "E289.103", {"start": v(-26.33, 26.63) * mm, "end": v(-27.53, 26.88) * mm});
            skLineSegment(sketch, "E289.104", {"start": v(-24.75, 25.97) * mm, "end": v(-26.33, 26.63) * mm});
            skLineSegment(sketch, "E289.105", {"start": v(-29.73, 27.16) * mm, "end": v(-31, 27.16) * mm});
            skLineSegment(sketch, "E289.106", {"start": v(-31, 27.16) * mm, "end": v(-32.79, 26.86) * mm});
            skLineSegment(sketch, "E289.107", {"start": v(-32.79, 26.86) * mm, "end": v(-34.44, 26.1) * mm});
            skLineSegment(sketch, "E289.108", {"start": v(-34.44, 26.1) * mm, "end": v(-35.75, 25.37) * mm});
            skLineSegment(sketch, "E289.109", {"start": v(-35.75, 25.37) * mm, "end": v(-37.02, 24.31) * mm});
            skLineSegment(sketch, "E289.110", {"start": v(-37.02, 24.31) * mm, "end": v(-38.66, 22.43) * mm});
            skLineSegment(sketch, "E289.111", {"start": v(-41.74, 4.56) * mm, "end": v(-43.35, 3.72) * mm});
            skLineSegment(sketch, "E289.112", {"start": v(-43.35, 3.72) * mm, "end": v(-44.59, 2.15) * mm});
            skLineSegment(sketch, "E289.113", {"start": v(-44.59, 2.15) * mm, "end": v(-45.56, 0.77) * mm});
            skLineSegment(sketch, "E289.114", {"start": v(-45.56, 0.77) * mm, "end": v(-46.22, -0.55) * mm});
            skLineSegment(sketch, "E289.115", {"start": v(-46.22, -0.55) * mm, "end": v(-46.93, -1.92) * mm});
            skLineSegment(sketch, "E289.116", {"start": v(-46.93, -1.92) * mm, "end": v(-47.57, -3.57) * mm});
            skLineSegment(sketch, "E289.117", {"start": v(-47.57, -3.57) * mm, "end": v(-47.9, -5.42) * mm});
            skLineSegment(sketch, "E289.118", {"start": v(-47.9, -5.42) * mm, "end": v(-47.9, -8) * mm});
            skLineSegment(sketch, "E289.119", {"start": v(-47.9, -8) * mm, "end": v(-47.8, -9.46) * mm});
            skLineSegment(sketch, "E289.120", {"start": v(-47.8, -9.46) * mm, "end": v(-47.57, -10.43) * mm});
            skLineSegment(sketch, "E289.121", {"start": v(-47.57, -10.43) * mm, "end": v(-47.22, -11.64) * mm});
            skLineSegment(sketch, "E289.122", {"start": v(-47.22, -11.64) * mm, "end": v(-46.7, -12.73) * mm});
            skLineSegment(sketch, "E289.123", {"start": v(-46.7, -12.73) * mm, "end": v(-45.71, -14.4) * mm});
            skLineSegment(sketch, "E289.124", {"start": v(-45.71, -14.4) * mm, "end": v(-44.51, -15.83) * mm});
            skLineSegment(sketch, "E289.125", {"start": v(-44.51, -15.83) * mm, "end": v(-43.46, -16.54) * mm});
            skLineSegment(sketch, "E289.126", {"start": v(-43.46, -16.54) * mm, "end": v(-42.14, -17.55) * mm});
            skLineSegment(sketch, "E289.127", {"start": v(-42.14, -17.55) * mm, "end": v(-40.86, -18.24) * mm});
            skLineSegment(sketch, "E289.128", {"start": v(-40.86, -18.24) * mm, "end": v(-39.83, -18.73) * mm});
            skLineSegment(sketch, "E289.129", {"start": v(-39.83, -18.73) * mm, "end": v(-38.33, -19.3) * mm});
            skLineSegment(sketch, "E289.130", {"start": v(-38.33, -19.3) * mm, "end": v(-37.13, -19.56) * mm});
            skLineSegment(sketch, "E289.131", {"start": v(-37.13, -19.56) * mm, "end": v(-35.74, -19.71) * mm});
            skLineSegment(sketch, "E289.132", {"start": v(-35.74, -19.71) * mm, "end": v(-34.03, -19.71) * mm});
            skLineSegment(sketch, "E289.135", {"start": v(33.29, -14.38) * mm, "end": v(33.84, -13.87) * mm});
            skLineSegment(sketch, "E289.136", {"start": v(33.84, -13.87) * mm, "end": v(34.26, -13.56) * mm});
            skLineSegment(sketch, "E289.137", {"start": v(34.26, -13.56) * mm, "end": v(34.82, -14.5) * mm});
            skLineSegment(sketch, "E289.138", {"start": v(34.82, -14.5) * mm, "end": v(35.85, -15.52) * mm});
            skLineSegment(sketch, "E289.139", {"start": v(35.85, -15.52) * mm, "end": v(36.73, -16.25) * mm});
            skLineSegment(sketch, "E289.140", {"start": v(36.73, -16.25) * mm, "end": v(38.01, -17.02) * mm});
            skLineSegment(sketch, "E289.141", {"start": v(38.01, -17.02) * mm, "end": v(39.29, -17.66) * mm});
            skLineSegment(sketch, "E289.142", {"start": v(39.29, -17.66) * mm, "end": v(40.9, -18.2) * mm});
            skLineSegment(sketch, "E289.143", {"start": v(40.9, -18.2) * mm, "end": v(41.85, -18.45) * mm});
            skLineSegment(sketch, "E289.147", {"start": v(47.82, -18.45) * mm, "end": v(49.1, -18.14) * mm});
            skLineSegment(sketch, "E289.148", {"start": v(49.1, -18.14) * mm, "end": v(50.3, -17.67) * mm});
            skLineSegment(sketch, "E289.149", {"start": v(50.3, -17.67) * mm, "end": v(52.1, -16.98) * mm});
            skLineSegment(sketch, "E289.150", {"start": v(52.1, -16.98) * mm, "end": v(53.63, -16.35) * mm});
            skLineSegment(sketch, "E289.151", {"start": v(53.63, -16.35) * mm, "end": v(55.26, -15.3) * mm});
            skLineSegment(sketch, "E289.152", {"start": v(55.26, -15.3) * mm, "end": v(56.4, -14.65) * mm});
            skLineSegment(sketch, "E289.153", {"start": v(56.4, -14.65) * mm, "end": v(58.06, -13.29) * mm});
            skLineSegment(sketch, "E289.154", {"start": v(58.06, -13.29) * mm, "end": v(59.54, -11.75) * mm});
            skLineSegment(sketch, "E289.155", {"start": v(59.54, -11.75) * mm, "end": v(60.85, -10.23) * mm});
            skLineSegment(sketch, "E289.156", {"start": v(60.85, -10.23) * mm, "end": v(61.78, -8.82) * mm});
            skLineSegment(sketch, "E289.157", {"start": v(61.78, -8.82) * mm, "end": v(62.79, -6.98) * mm});
            skLineSegment(sketch, "E289.158", {"start": v(62.79, -6.98) * mm, "end": v(63.73, -4.99) * mm});
            skLineSegment(sketch, "E289.159", {"start": v(63.73, -4.99) * mm, "end": v(64.45, -2.57) * mm});
            skLineSegment(sketch, "E289.160", {"start": v(64.45, -2.57) * mm, "end": v(64.6, -1.56) * mm});
            skLineSegment(sketch, "E289.161", {"start": v(64.6, -1.56) * mm, "end": v(64.6, 0.89) * mm});
            skLineSegment(sketch, "E289.162", {"start": v(64.6, 0.89) * mm, "end": v(64.38, 1.75) * mm});
            skLineSegment(sketch, "E289.163", {"start": v(64.38, 1.75) * mm, "end": v(63.8, 2.73) * mm});
            skLineSegment(sketch, "E289.164", {"start": v(63.8, 2.73) * mm, "end": v(62.9, 3.54) * mm});
            skLineSegment(sketch, "E289.165", {"start": v(62.9, 3.54) * mm, "end": v(61.48, 3.72) * mm});
            skLineSegment(sketch, "E289.171", {"start": v(60.98, 6.85) * mm, "end": v(61.18, 8.48) * mm});
            skLineSegment(sketch, "E289.172", {"start": v(61.18, 8.48) * mm, "end": v(60.98, 9.66) * mm});
            skLineSegment(sketch, "E289.173", {"start": v(60.98, 9.66) * mm, "end": v(60.78, 10.65) * mm});
            skLineSegment(sketch, "E289.174", {"start": v(60.78, 10.65) * mm, "end": v(60.48, 11.76) * mm});
            skLineSegment(sketch, "E289.175", {"start": v(60.48, 11.76) * mm, "end": v(60.06, 12.6) * mm});
            skLineSegment(sketch, "E289.176", {"start": v(60.06, 12.6) * mm, "end": v(59.47, 13.54) * mm});
            skLineSegment(sketch, "E289.177", {"start": v(59.47, 13.54) * mm, "end": v(58.57, 14.82) * mm});
            skLineSegment(sketch, "E289.178", {"start": v(58.57, 14.82) * mm, "end": v(57.73, 15.87) * mm});
            skLineSegment(sketch, "E289.179", {"start": v(57.73, 15.87) * mm, "end": v(56.53, 17.04) * mm});
            skLineSegment(sketch, "E289.180", {"start": v(56.53, 17.04) * mm, "end": v(54.94, 17.82) * mm});
            skLineSegment(sketch, "E289.181", {"start": v(54.94, 17.82) * mm, "end": v(53.76, 18.28) * mm});
            skLineSegment(sketch, "E289.182", {"start": v(53.76, 18.28) * mm, "end": v(52.85, 18.52) * mm});
            skLineSegment(sketch, "E289.183", {"start": v(52.85, 18.52) * mm, "end": v(52.27, 18.6) * mm});
            skLineSegment(sketch, "E289.184", {"start": v(52.27, 18.6) * mm, "end": v(51.69, 18.66) * mm});
            skLineSegment(sketch, "E289.185", {"start": v(51.69, 18.66) * mm, "end": v(51.17, 18.62) * mm});
            skLineSegment(sketch, "E289.186", {"start": v(51.17, 18.62) * mm, "end": v(50.53, 18.52) * mm});
            skLineSegment(sketch, "E289.187", {"start": v(50.53, 18.52) * mm, "end": v(49.9, 18.4) * mm});
            skLineSegment(sketch, "E289.188", {"start": v(49.9, 18.4) * mm, "end": v(49, 18.13) * mm});
            skLineSegment(sketch, "E289.189", {"start": v(49, 18.13) * mm, "end": v(47.38, 17.54) * mm});
            skLineSegment(sketch, "E289.190", {"start": v(47.38, 17.54) * mm, "end": v(46.13, 16.94) * mm});
            skLineSegment(sketch, "E289.191", {"start": v(46.13, 16.94) * mm, "end": v(45.83, 16.75) * mm});
            skLineSegment(sketch, "E289.192", {"start": v(45.83, 16.75) * mm, "end": v(45.57, 17.08) * mm});
            skLineSegment(sketch, "E289.193", {"start": v(45.57, 17.08) * mm, "end": v(44.98, 17.67) * mm});
            skLineSegment(sketch, "E289.194", {"start": v(44.98, 17.67) * mm, "end": v(43.97, 18.35) * mm});
            skLineSegment(sketch, "E289.195", {"start": v(43.97, 18.35) * mm, "end": v(42.94, 18.73) * mm});
            skLineSegment(sketch, "E289.196", {"start": v(42.94, 18.73) * mm, "end": v(42, 18.88) * mm});
            skLineSegment(sketch, "E289.197", {"start": v(42, 18.88) * mm, "end": v(40.69, 18.97) * mm});
            skLineSegment(sketch, "E289.198", {"start": v(40.69, 18.97) * mm, "end": v(39.49, 19.07) * mm});
            skLineSegment(sketch, "E289.202", {"start": v(39.22, 21.91) * mm, "end": v(37.93, 22.93) * mm});
            skLineSegment(sketch, "E289.203", {"start": v(37.93, 22.93) * mm, "end": v(36.68, 23.5) * mm});
            skLineSegment(sketch, "E289.204", {"start": v(36.68, 23.5) * mm, "end": v(35.67, 23.63) * mm});
            skLineSegment(sketch, "E289.205", {"start": v(35.67, 23.63) * mm, "end": v(34.87, 23.54) * mm});
            skLineSegment(sketch, "E289.206", {"start": v(34.87, 23.54) * mm, "end": v(33.77, 23.43) * mm});
            skLineSegment(sketch, "E289.207", {"start": v(33.77, 23.43) * mm, "end": v(32.8, 23.23) * mm});
            skLineSegment(sketch, "E289.208", {"start": v(32.8, 23.23) * mm, "end": v(31.56, 22.56) * mm});
            skLineSegment(sketch, "E289.209", {"start": v(31.56, 22.56) * mm, "end": v(26.84, 19.4) * mm});
            skLineSegment(sketch, "E289.210", {"start": v(26.84, 19.4) * mm, "end": v(26.36, 19.24) * mm});
            skLineSegment(sketch, "E289.211", {"start": v(26.36, 19.24) * mm, "end": v(26.17, 19.24) * mm});
            skLineSegment(sketch, "E289.212", {"start": v(26.17, 19.24) * mm, "end": v(25.67, 19.3) * mm});
            skLineSegment(sketch, "E289.213", {"start": v(25.67, 19.3) * mm, "end": v(25.51, 19.37) * mm});
            skLineSegment(sketch, "E289.214", {"start": v(25.51, 19.37) * mm, "end": v(20.88, 22.35) * mm});
            skLineSegment(sketch, "E289.215", {"start": v(20.88, 22.35) * mm, "end": v(19.88, 23.14) * mm});
            skLineSegment(sketch, "E289.216", {"start": v(19.88, 23.14) * mm, "end": v(18.93, 23.58) * mm});
            skLineSegment(sketch, "E289.217", {"start": v(18.93, 23.58) * mm, "end": v(17.83, 23.72) * mm});
            skLineSegment(sketch, "E289.218", {"start": v(17.83, 23.72) * mm, "end": v(17.1, 23.72) * mm});
            skLineSegment(sketch, "E289.219", {"start": v(17.1, 23.72) * mm, "end": v(16.3, 23.6) * mm});
            skLineSegment(sketch, "E289.220", {"start": v(16.3, 23.6) * mm, "end": v(15.6, 23.42) * mm});
            skLineSegment(sketch, "E289.221", {"start": v(15.6, 23.42) * mm, "end": v(14.82, 22.8) * mm});
            skLineSegment(sketch, "E289.222", {"start": v(14.82, 22.8) * mm, "end": v(14.37, 22.14) * mm});
            skLineSegment(sketch, "E289.223", {"start": v(14.37, 22.14) * mm, "end": v(14.09, 21.53) * mm});
            skLineSegment(sketch, "E289.224", {"start": v(14.09, 21.53) * mm, "end": v(13.92, 20.83) * mm});
            skLineSegment(sketch, "E289.225", {"start": v(13.92, 20.83) * mm, "end": v(13.71, 20.03) * mm});
            skLineSegment(sketch, "E289.226", {"start": v(13.71, 20.03) * mm, "end": v(13.57, 18.9) * mm});
            skLineSegment(sketch, "E289.227", {"start": v(13.57, 18.9) * mm, "end": v(12.31, 18.9) * mm});
            skLineSegment(sketch, "E289.228", {"start": v(12.31, 18.9) * mm, "end": v(11.7, 19.17) * mm});
            skLineSegment(sketch, "E289.229", {"start": v(12.14, 18.97) * mm, "end": v(11.7, 19.17) * mm});
            skLineSegment(sketch, "E289.230", {"start": v(12.14, 18.97) * mm, "end": v(11.95, 19.13) * mm});
            skLineSegment(sketch, "E289.231", {"start": v(11.95, 19.13) * mm, "end": v(11.6, 19.48) * mm});
            skLineSegment(sketch, "E289.232", {"start": v(11.6, 19.48) * mm, "end": v(11.26, 19.9) * mm});
            skLineSegment(sketch, "E289.233", {"start": v(11.26, 19.9) * mm, "end": v(10.92, 20.42) * mm});
            skLineSegment(sketch, "E289.234", {"start": v(10.92, 20.42) * mm, "end": v(10.6, 21.02) * mm});
            skLineSegment(sketch, "E289.235", {"start": v(10.6, 21.02) * mm, "end": v(9.68, 22.15) * mm});
            skLineSegment(sketch, "E289.236", {"start": v(9.68, 22.15) * mm, "end": v(9.06, 22.78) * mm});
            skLineSegment(sketch, "E290", {"start": v(-39.2, 5.3) * mm, "end": v(-41.74, 4.56) * mm});
            skLineSegment(sketch, "E291", {"start": v(-41.37, 11.72) * mm, "end": v(-40.43, 8.52) * mm});
            skLineSegment(sketch, "E292", {"start": v(-41.37, 15.23) * mm, "end": v(-41.37, 11.72) * mm});
            skLineSegment(sketch, "E293", {"start": v(-27.5, -17.9) * mm, "end": v(-29.94, -18.99) * mm});
            skLineSegment(sketch, "E294", {"start": v(-31.42, -19.42) * mm, "end": v(-34.03, -19.71) * mm});
            skLineSegment(sketch, "E295", {"start": v(30.67, -17.04) * mm, "end": v(32.16, -15.68) * mm});
            skLineSegment(sketch, "E296", {"start": v(41.85, -18.45) * mm, "end": v(47.82, -18.45) * mm});
            skLineSegment(sketch, "E297", {"start": v(60.15, 3.72) * mm, "end": v(60.98, 6.85) * mm});
            skLineSegment(sketch, "E298", {"start": v(39.22, 21.91) * mm, "end": v(39.49, 19.07) * mm});
            skLineSegment(sketch, "E299", {"start": v(60.15, 3.72) * mm, "end": v(61.48, 3.72) * mm});
            skSolve(sketch);
        }
        {
            var Q0;
            Q0=qCreatedBy(makeId("Top.planeOp"),FACE);
            var sketch = newSketch(context, id + "F2", { "sketchPlane" : qUnion([Q0])});
            skLineSegment(sketch, "E300.0", {"start": v(67.68, 5.95) * mm, "end": v(66.08, 7.4) * mm});
            skLineSegment(sketch, "E300.1", {"start": v(69.06, 3.68) * mm, "end": v(67.68, 5.95) * mm});
            skLineSegment(sketch, "E300.2", {"start": v(69.6, 1.48) * mm, "end": v(69.06, 3.68) * mm});
            skLineSegment(sketch, "E300.3", {"start": v(69.6, -1.92) * mm, "end": v(69.6, 1.48) * mm});
            skLineSegment(sketch, "E300.4", {"start": v(69.35, -3.64) * mm, "end": v(69.6, -1.92) * mm});
            skLineSegment(sketch, "E300.5", {"start": v(68.41, -6.78) * mm, "end": v(69.35, -3.64) * mm});
            skLineSegment(sketch, "E300.6", {"start": v(67.25, -9.25) * mm, "end": v(68.41, -6.78) * mm});
            skLineSegment(sketch, "E300.7", {"start": v(66.07, -11.4) * mm, "end": v(67.25, -9.25) * mm});
            skLineSegment(sketch, "E300.8", {"start": v(64.84, -13.26) * mm, "end": v(66.07, -11.4) * mm});
            skLineSegment(sketch, "E300.9", {"start": v(63.23, -15.12) * mm, "end": v(64.84, -13.26) * mm});
            skLineSegment(sketch, "E300.10", {"start": v(61.45, -16.97) * mm, "end": v(63.23, -15.12) * mm});
            skLineSegment(sketch, "E300.11", {"start": v(59.22, -18.8) * mm, "end": v(61.45, -16.97) * mm});
            skLineSegment(sketch, "E300.12", {"start": v(57.85, -19.57) * mm, "end": v(59.22, -18.8) * mm});
            skLineSegment(sketch, "E300.13", {"start": v(55.96, -20.8) * mm, "end": v(57.85, -19.57) * mm});
            skLineSegment(sketch, "E300.14", {"start": v(53.94, -21.63) * mm, "end": v(55.96, -20.8) * mm});
            skLineSegment(sketch, "E300.15", {"start": v(52.12, -22.33) * mm, "end": v(53.94, -21.63) * mm});
            skLineSegment(sketch, "E300.16", {"start": v(50.6, -22.92) * mm, "end": v(52.12, -22.33) * mm});
            skLineSegment(sketch, "E300.17", {"start": v(48.42, -23.45) * mm, "end": v(50.6, -22.92) * mm});
            skLineSegment(sketch, "E300.18", {"start": v(41.21, -23.45) * mm, "end": v(48.42, -23.45) * mm});
            skLineSegment(sketch, "E300.19", {"start": v(39.47, -23) * mm, "end": v(41.21, -23.45) * mm});
            skLineSegment(sketch, "E300.20", {"start": v(37.36, -22.28) * mm, "end": v(39.47, -23) * mm});
            skLineSegment(sketch, "E300.21", {"start": v(35.6, -21.4) * mm, "end": v(37.36, -22.28) * mm});
            skLineSegment(sketch, "E300.22", {"start": v(34.22, -20.57) * mm, "end": v(35.6, -21.4) * mm});
            skLineSegment(sketch, "E300.23", {"start": v(33.46, -21.26) * mm, "end": v(34.22, -20.57) * mm});
            skLineSegment(sketch, "E300.24", {"start": v(31.73, -22.05) * mm, "end": v(33.46, -21.26) * mm});
            skLineSegment(sketch, "E300.25", {"start": v(30.8, -22.5) * mm, "end": v(31.73, -22.05) * mm});
            skLineSegment(sketch, "E300.26", {"start": v(28.7, -23.2) * mm, "end": v(30.8, -22.5) * mm});
            skLineSegment(sketch, "E300.27", {"start": v(25.1, -23.2) * mm, "end": v(28.7, -23.2) * mm});
            skLineSegment(sketch, "E300.28", {"start": v(22.64, -22.33) * mm, "end": v(25.1, -23.2) * mm});
            skLineSegment(sketch, "E300.29", {"start": v(20.56, -21.48) * mm, "end": v(22.64, -22.33) * mm});
            skLineSegment(sketch, "E300.30", {"start": v(19.75, -22.25) * mm, "end": v(20.56, -21.48) * mm});
            skLineSegment(sketch, "E300.31", {"start": v(18.52, -23.38) * mm, "end": v(19.75, -22.25) * mm});
            skLineSegment(sketch, "E300.32", {"start": v(16.93, -24.6) * mm, "end": v(18.52, -23.38) * mm});
            skLineSegment(sketch, "E300.33", {"start": v(15.54, -25.48) * mm, "end": v(16.93, -24.6) * mm});
            skLineSegment(sketch, "E300.34", {"start": v(14.52, -26.05) * mm, "end": v(15.54, -25.48) * mm});
            skLineSegment(sketch, "E300.35", {"start": v(13.38, -26.62) * mm, "end": v(14.52, -26.05) * mm});
            skLineSegment(sketch, "E300.36", {"start": v(12.38, -27.02) * mm, "end": v(13.38, -26.62) * mm});
            skLineSegment(sketch, "E300.37", {"start": v(10.89, -27.58) * mm, "end": v(12.38, -27.02) * mm});
            skLineSegment(sketch, "E300.38", {"start": v(9.08, -28.17) * mm, "end": v(10.89, -27.58) * mm});
            skLineSegment(sketch, "E300.39", {"start": v(7.3, -28.63) * mm, "end": v(9.08, -28.17) * mm});
            skLineSegment(sketch, "E300.40", {"start": v(5.54, -28.89) * mm, "end": v(7.3, -28.63) * mm});
            skLineSegment(sketch, "E300.41", {"start": v(3.34, -29.1) * mm, "end": v(5.54, -28.89) * mm});
            skLineSegment(sketch, "E300.42", {"start": v(-0.01, -29.31) * mm, "end": v(3.34, -29.1) * mm});
            skLineSegment(sketch, "E300.43", {"start": v(-3.5, -29.07) * mm, "end": v(-0.01, -29.31) * mm});
            skLineSegment(sketch, "E300.44", {"start": v(-7.27, -28.36) * mm, "end": v(-3.5, -29.07) * mm});
            skLineSegment(sketch, "E300.45", {"start": v(-10.6, -27.5) * mm, "end": v(-7.27, -28.36) * mm});
            skLineSegment(sketch, "E300.46", {"start": v(-13.64, -26.53) * mm, "end": v(-10.6, -27.5) * mm});
            skLineSegment(sketch, "E300.47", {"start": v(-15.69, -25.53) * mm, "end": v(-13.64, -26.53) * mm});
            skLineSegment(sketch, "E300.48", {"start": v(-17.45, -24.58) * mm, "end": v(-15.69, -25.53) * mm});
            skLineSegment(sketch, "E300.49", {"start": v(66.08, 7.4) * mm, "end": v(66.23, 8.6) * mm});
            skLineSegment(sketch, "E300.50", {"start": v(-18.93, -23.79) * mm, "end": v(-17.45, -24.58) * mm});
            skLineSegment(sketch, "E300.51", {"start": v(-21.8, -22.25) * mm, "end": v(-18.93, -23.79) * mm});
            skLineSegment(sketch, "E300.52", {"start": v(-23.24, -21.14) * mm, "end": v(-21.8, -22.25) * mm});
            skLineSegment(sketch, "E300.53", {"start": v(-23.99, -21.69) * mm, "end": v(-23.24, -21.14) * mm});
            skLineSegment(sketch, "E300.54", {"start": v(-25.27, -22.4) * mm, "end": v(-23.99, -21.69) * mm});
            skLineSegment(sketch, "E300.55", {"start": v(-28.22, -23.7) * mm, "end": v(-25.27, -22.4) * mm});
            skLineSegment(sketch, "E300.56", {"start": v(-30.42, -24.34) * mm, "end": v(-28.22, -23.7) * mm});
            skLineSegment(sketch, "E300.57", {"start": v(-33.75, -24.71) * mm, "end": v(-30.42, -24.34) * mm});
            skLineSegment(sketch, "E300.58", {"start": v(-36, -24.71) * mm, "end": v(-33.75, -24.71) * mm});
            skLineSegment(sketch, "E300.59", {"start": v(-37.95, -24.5) * mm, "end": v(-36, -24.71) * mm});
            skLineSegment(sketch, "E300.60", {"start": v(-39.76, -24.1) * mm, "end": v(-37.95, -24.5) * mm});
            skLineSegment(sketch, "E300.61", {"start": v(-41.78, -23.34) * mm, "end": v(-39.76, -24.1) * mm});
            skLineSegment(sketch, "E300.62", {"start": v(-43.12, -22.7) * mm, "end": v(-41.78, -23.34) * mm});
            skLineSegment(sketch, "E300.63", {"start": v(-44.86, -21.76) * mm, "end": v(-43.12, -22.7) * mm});
            skLineSegment(sketch, "E300.64", {"start": v(-46.38, -20.6) * mm, "end": v(-44.86, -21.76) * mm});
            skLineSegment(sketch, "E300.65", {"start": v(-0.66, 32.44) * mm, "end": v(-1.55, 33.73) * mm});
            skLineSegment(sketch, "E300.66", {"start": v(0.32, 30.63) * mm, "end": v(-0.66, 32.44) * mm});
            skLineSegment(sketch, "E300.67", {"start": v(0.9, 29.05) * mm, "end": v(0.32, 30.63) * mm});
            skLineSegment(sketch, "E300.68", {"start": v(0.94, 28.9) * mm, "end": v(0.9, 29.05) * mm});
            skLineSegment(sketch, "E300.69", {"start": v(7.2, 28.9) * mm, "end": v(0.94, 28.9) * mm});
            skLineSegment(sketch, "E300.70", {"start": v(8.92, 28.48) * mm, "end": v(7.2, 28.9) * mm});
            skLineSegment(sketch, "E300.71", {"start": v(10.4, 27.8) * mm, "end": v(8.92, 28.48) * mm});
            skLineSegment(sketch, "E300.72", {"start": v(11.93, 26.88) * mm, "end": v(10.4, 27.8) * mm});
            skLineSegment(sketch, "E300.73", {"start": v(13.33, 28.02) * mm, "end": v(11.93, 26.88) * mm});
            skLineSegment(sketch, "E300.74", {"start": v(15.32, 28.5) * mm, "end": v(13.33, 28.02) * mm});
            skLineSegment(sketch, "E300.75", {"start": v(16.71, 28.72) * mm, "end": v(15.32, 28.5) * mm});
            skLineSegment(sketch, "E300.76", {"start": v(18.14, 28.72) * mm, "end": v(16.71, 28.72) * mm});
            skLineSegment(sketch, "E300.77", {"start": v(20.3, 28.45) * mm, "end": v(18.14, 28.72) * mm});
            skLineSegment(sketch, "E300.78", {"start": v(22.51, 27.44) * mm, "end": v(20.3, 28.45) * mm});
            skLineSegment(sketch, "E300.79", {"start": v(23.8, 26.43) * mm, "end": v(22.51, 27.44) * mm});
            skLineSegment(sketch, "E300.80", {"start": v(26.11, 24.93) * mm, "end": v(23.8, 26.43) * mm});
            skLineSegment(sketch, "E300.81", {"start": v(28.99, 26.85) * mm, "end": v(26.11, 24.93) * mm});
            skLineSegment(sketch, "E300.82", {"start": v(31.07, 27.97) * mm, "end": v(28.99, 26.85) * mm});
            skLineSegment(sketch, "E300.83", {"start": v(33, 28.38) * mm, "end": v(31.07, 27.97) * mm});
            skLineSegment(sketch, "E300.84", {"start": v(34.34, 28.5) * mm, "end": v(33, 28.38) * mm});
            skLineSegment(sketch, "E300.85", {"start": v(35.68, 28.67) * mm, "end": v(34.34, 28.5) * mm});
            skLineSegment(sketch, "E300.86", {"start": v(38.06, 28.37) * mm, "end": v(35.68, 28.67) * mm});
            skLineSegment(sketch, "E300.87", {"start": v(40.56, 27.23) * mm, "end": v(38.06, 28.37) * mm});
            skLineSegment(sketch, "E300.88", {"start": v(44, 24.5) * mm, "end": v(40.56, 27.23) * mm});
            skLineSegment(sketch, "E300.89", {"start": v(56.95, 22.4) * mm, "end": v(55.3, 23.04) * mm});
            skLineSegment(sketch, "E300.90", {"start": v(59.45, 21.18) * mm, "end": v(56.95, 22.4) * mm});
            skLineSegment(sketch, "E300.91", {"start": v(61.44, 19.24) * mm, "end": v(59.45, 21.18) * mm});
            skLineSegment(sketch, "E300.92", {"start": v(62.58, 17.83) * mm, "end": v(61.44, 19.24) * mm});
            skLineSegment(sketch, "E300.93", {"start": v(63.65, 16.29) * mm, "end": v(62.58, 17.83) * mm});
            skLineSegment(sketch, "E300.94", {"start": v(64.43, 15.04) * mm, "end": v(63.65, 16.29) * mm});
            skLineSegment(sketch, "E300.95", {"start": v(66.23, 8.6) * mm, "end": v(65.9, 10.57) * mm});
            skLineSegment(sketch, "E300.96", {"start": v(65.9, 10.57) * mm, "end": v(65.65, 11.8) * mm});
            skLineSegment(sketch, "E300.97", {"start": v(65.65, 11.8) * mm, "end": v(65.17, 13.56) * mm});
            skLineSegment(sketch, "E300.98", {"start": v(65.17, 13.56) * mm, "end": v(64.43, 15.04) * mm});
            skLineSegment(sketch, "E300.99", {"start": v(55.3, 23.04) * mm, "end": v(53.8, 23.44) * mm});
            skLineSegment(sketch, "E300.100", {"start": v(53.8, 23.44) * mm, "end": v(52.86, 23.56) * mm});
            skLineSegment(sketch, "E300.101", {"start": v(52.86, 23.56) * mm, "end": v(51.8, 23.67) * mm});
            skLineSegment(sketch, "E300.102", {"start": v(51.8, 23.67) * mm, "end": v(50.62, 23.6) * mm});
            skLineSegment(sketch, "E300.103", {"start": v(50.62, 23.6) * mm, "end": v(49.63, 23.44) * mm});
            skLineSegment(sketch, "E300.104", {"start": v(49.63, 23.44) * mm, "end": v(48.71, 23.25) * mm});
            skLineSegment(sketch, "E300.105", {"start": v(48.71, 23.25) * mm, "end": v(47.44, 22.89) * mm});
            skLineSegment(sketch, "E300.106", {"start": v(47.44, 22.89) * mm, "end": v(46.63, 22.59) * mm});
            skLineSegment(sketch, "E300.107", {"start": v(46.63, 22.59) * mm, "end": v(46.28, 22.82) * mm});
            skLineSegment(sketch, "E300.108", {"start": v(46.28, 22.82) * mm, "end": v(44.22, 23.6) * mm});
            skLineSegment(sketch, "E300.109", {"start": v(44.22, 23.6) * mm, "end": v(44.08, 23.61) * mm});
            skLineSegment(sketch, "E300.110", {"start": v(44.08, 23.61) * mm, "end": v(44, 24.5) * mm});
            skLineSegment(sketch, "E300.111", {"start": v(-1.55, 33.73) * mm, "end": v(-2.63, 34.99) * mm});
            skLineSegment(sketch, "E300.112", {"start": v(-2.63, 34.99) * mm, "end": v(-3.95, 36.2) * mm});
            skLineSegment(sketch, "E300.113", {"start": v(-3.95, 36.2) * mm, "end": v(-5.16, 36.97) * mm});
            skLineSegment(sketch, "E300.114", {"start": v(-5.16, 36.97) * mm, "end": v(-6.93, 38.1) * mm});
            skLineSegment(sketch, "E300.115", {"start": v(-6.93, 38.1) * mm, "end": v(-8.68, 38.5) * mm});
            skLineSegment(sketch, "E300.116", {"start": v(-8.68, 38.5) * mm, "end": v(-9.68, 38.8) * mm});
            skLineSegment(sketch, "E300.117", {"start": v(-9.68, 38.8) * mm, "end": v(-11.06, 39.14) * mm});
            skLineSegment(sketch, "E300.118", {"start": v(-11.06, 39.14) * mm, "end": v(-12.86, 39.14) * mm});
            skLineSegment(sketch, "E300.119", {"start": v(-12.86, 39.14) * mm, "end": v(-13.92, 39.03) * mm});
            skLineSegment(sketch, "E300.120", {"start": v(-13.92, 39.03) * mm, "end": v(-14.61, 38.95) * mm});
            skLineSegment(sketch, "E300.121", {"start": v(-14.61, 38.95) * mm, "end": v(-16.17, 38.76) * mm});
            skLineSegment(sketch, "E300.122", {"start": v(-16.17, 38.76) * mm, "end": v(-17.54, 38.3) * mm});
            skLineSegment(sketch, "E300.123", {"start": v(-17.54, 38.3) * mm, "end": v(-18.45, 37.97) * mm});
            skLineSegment(sketch, "E300.124", {"start": v(-18.45, 37.97) * mm, "end": v(-19.53, 37.57) * mm});
            skLineSegment(sketch, "E300.125", {"start": v(-19.53, 37.57) * mm, "end": v(-20.8, 36.91) * mm});
            skLineSegment(sketch, "E300.126", {"start": v(-20.8, 36.91) * mm, "end": v(-21.94, 36.19) * mm});
            skLineSegment(sketch, "E300.127", {"start": v(-21.94, 36.19) * mm, "end": v(-23.1, 35.32) * mm});
            skLineSegment(sketch, "E300.128", {"start": v(-23.1, 35.32) * mm, "end": v(-24.32, 34.16) * mm});
            skLineSegment(sketch, "E300.129", {"start": v(-24.32, 34.16) * mm, "end": v(-24.88, 33.56) * mm});
            skLineSegment(sketch, "E300.130", {"start": v(-24.88, 33.56) * mm, "end": v(-25.6, 32.74) * mm});
            skLineSegment(sketch, "E300.131", {"start": v(-25.6, 32.74) * mm, "end": v(-26.4, 31.76) * mm});
            skLineSegment(sketch, "E300.132", {"start": v(-26.4, 31.76) * mm, "end": v(-26.69, 31.81) * mm});
            skLineSegment(sketch, "E300.133", {"start": v(-26.69, 31.81) * mm, "end": v(-27.93, 31.98) * mm});
            skLineSegment(sketch, "E300.134", {"start": v(-27.93, 31.98) * mm, "end": v(-29.43, 32.16) * mm});
            skLineSegment(sketch, "E300.135", {"start": v(-29.43, 32.16) * mm, "end": v(-31.41, 32.16) * mm});
            skLineSegment(sketch, "E300.136", {"start": v(-31.41, 32.16) * mm, "end": v(-34.27, 31.69) * mm});
            skLineSegment(sketch, "E300.137", {"start": v(-34.27, 31.69) * mm, "end": v(-36.7, 30.56) * mm});
            skLineSegment(sketch, "E300.138", {"start": v(-36.7, 30.56) * mm, "end": v(-38.6, 29.51) * mm});
            skLineSegment(sketch, "E300.139", {"start": v(-38.6, 29.51) * mm, "end": v(-40.53, 27.9) * mm});
            skLineSegment(sketch, "E300.140", {"start": v(-40.53, 27.9) * mm, "end": v(-42.65, 25.46) * mm});
            skLineSegment(sketch, "E300.141", {"start": v(-42.65, 25.46) * mm, "end": v(-44.48, 22.68) * mm});
            skLineSegment(sketch, "E300.142", {"start": v(-44.48, 22.68) * mm, "end": v(-45.97, 19.12) * mm});
            skLineSegment(sketch, "E300.143", {"start": v(-45.97, 19.12) * mm, "end": v(-46.37, 15.5) * mm});
            skLineSegment(sketch, "E300.144", {"start": v(-46.37, 15.5) * mm, "end": v(-46.37, 11) * mm});
            skLineSegment(sketch, "E300.145", {"start": v(-46.37, 11) * mm, "end": v(-45.55, 8.21) * mm});
            skLineSegment(sketch, "E300.146", {"start": v(-45.55, 8.21) * mm, "end": v(-46.62, 7.65) * mm});
            skLineSegment(sketch, "E300.147", {"start": v(-46.62, 7.65) * mm, "end": v(-48.6, 5.14) * mm});
            skLineSegment(sketch, "E300.148", {"start": v(-48.6, 5.14) * mm, "end": v(-49.87, 3.34) * mm});
            skLineSegment(sketch, "E300.149", {"start": v(-49.87, 3.34) * mm, "end": v(-50.67, 1.72) * mm});
            skLineSegment(sketch, "E300.150", {"start": v(-50.67, 1.72) * mm, "end": v(-51.5, 0.15) * mm});
            skLineSegment(sketch, "E300.151", {"start": v(-51.5, 0.15) * mm, "end": v(-52.4, -2.2) * mm});
            skLineSegment(sketch, "E300.152", {"start": v(-52.4, -2.2) * mm, "end": v(-52.9, -4.97) * mm});
            skLineSegment(sketch, "E300.153", {"start": v(-52.9, -4.97) * mm, "end": v(-52.9, -8.19) * mm});
            skLineSegment(sketch, "E300.154", {"start": v(-52.9, -8.19) * mm, "end": v(-52.76, -10.23) * mm});
            skLineSegment(sketch, "E300.155", {"start": v(-52.76, -10.23) * mm, "end": v(-52.4, -11.7) * mm});
            skLineSegment(sketch, "E300.156", {"start": v(-52.4, -11.7) * mm, "end": v(-51.9, -13.43) * mm});
            skLineSegment(sketch, "E300.157", {"start": v(-51.9, -13.43) * mm, "end": v(-51.1, -15.09) * mm});
            skLineSegment(sketch, "E300.158", {"start": v(-51.1, -15.09) * mm, "end": v(-49.81, -17.29) * mm});
            skLineSegment(sketch, "E300.159", {"start": v(-49.81, -17.29) * mm, "end": v(-47.9, -19.58) * mm});
            skLineSegment(sketch, "E300.160", {"start": v(-47.9, -19.58) * mm, "end": v(-46.38, -20.6) * mm});
            skSolve(sketch);
        }
        {
            var Q0;
            Q0=makeQuery(id+"F2.imprint","IMPRINT",FACE,{"disambiguationData":[TD([[makeQuery(id+"F2.imprint","IMPRINT",EDGE,{"derivedFrom":sQuery(id+"F2.wireOp",EDGE,"E300.0")}),1.0]])]});
            extrude(context, id + "F3", {"entities" : qUnion([Q0]), "depth" : 63 * mm, "offsetDistance" : 25 * mm});
        }
        {
            var Q0;
            Q0=qCreatedBy(makeId("Right.planeOp"),FACE);
            cPlane(context, id + "F4", {"entities" : qUnion([Q0]), "cplaneType" : CPlaneType.OFFSET, "offset" : 55.6 * mm, "oppositeDirection" : true, "width" : 150 * mm, "height" : 150 * mm});
        }
        {
            var Q0;
            Q0=makeQuery(id+"F3.opExtrude","CAP_FACE",FACE,{"disambiguationData":[OSD([sQuery(id+"F2.wireOp",EDGE,"E300.0"),sQuery(id+"F2.wireOp",EDGE,"E300.1"),sQuery(id+"F2.wireOp",EDGE,"E300.2"),sQuery(id+"F2.wireOp",EDGE,"E300.3"),sQuery(id+"F2.wireOp",EDGE,"E300.4"),sQuery(id+"F2.wireOp",EDGE,"E300.5"),sQuery(id+"F2.wireOp",EDGE,"E300.6"),sQuery(id+"F2.wireOp",EDGE,"E300.7"),sQuery(id+"F2.wireOp",EDGE,"E300.8"),sQuery(id+"F2.wireOp",EDGE,"E300.9"),sQuery(id+"F2.wireOp",EDGE,"E300.10"),sQuery(id+"F2.wireOp",EDGE,"E300.11"),sQuery(id+"F2.wireOp",EDGE,"E300.12"),sQuery(id+"F2.wireOp",EDGE,"E300.13"),sQuery(id+"F2.wireOp",EDGE,"E300.14"),sQuery(id+"F2.wireOp",EDGE,"E300.15"),sQuery(id+"F2.wireOp",EDGE,"E300.16"),sQuery(id+"F2.wireOp",EDGE,"E300.17"),sQuery(id+"F2.wireOp",EDGE,"E300.18"),sQuery(id+"F2.wireOp",EDGE,"E300.19"),sQuery(id+"F2.wireOp",EDGE,"E300.20"),sQuery(id+"F2.wireOp",EDGE,"E300.21"),sQuery(id+"F2.wireOp",EDGE,"E300.22"),sQuery(id+"F2.wireOp",EDGE,"E300.23"),sQuery(id+"F2.wireOp",EDGE,"E300.24"),sQuery(id+"F2.wireOp",EDGE,"E300.25"),sQuery(id+"F2.wireOp",EDGE,"E300.26"),sQuery(id+"F2.wireOp",EDGE,"E300.27"),sQuery(id+"F2.wireOp",EDGE,"E300.28"),sQuery(id+"F2.wireOp",EDGE,"E300.29"),sQuery(id+"F2.wireOp",EDGE,"E300.30"),sQuery(id+"F2.wireOp",EDGE,"E300.31"),sQuery(id+"F2.wireOp",EDGE,"E300.32"),sQuery(id+"F2.wireOp",EDGE,"E300.33"),sQuery(id+"F2.wireOp",EDGE,"E300.34"),sQuery(id+"F2.wireOp",EDGE,"E300.35"),sQuery(id+"F2.wireOp",EDGE,"E300.36"),sQuery(id+"F2.wireOp",EDGE,"E300.37"),sQuery(id+"F2.wireOp",EDGE,"E300.38"),sQuery(id+"F2.wireOp",EDGE,"E300.39"),sQuery(id+"F2.wireOp",EDGE,"E300.40"),sQuery(id+"F2.wireOp",EDGE,"E300.41"),sQuery(id+"F2.wireOp",EDGE,"E300.42"),sQuery(id+"F2.wireOp",EDGE,"E300.43"),sQuery(id+"F2.wireOp",EDGE,"E300.44"),sQuery(id+"F2.wireOp",EDGE,"E300.45"),sQuery(id+"F2.wireOp",EDGE,"E300.46"),sQuery(id+"F2.wireOp",EDGE,"E300.47"),sQuery(id+"F2.wireOp",EDGE,"E300.48"),sQuery(id+"F2.wireOp",EDGE,"E300.49"),sQuery(id+"F2.wireOp",EDGE,"E300.50"),sQuery(id+"F2.wireOp",EDGE,"E300.51"),sQuery(id+"F2.wireOp",EDGE,"E300.52"),sQuery(id+"F2.wireOp",EDGE,"E300.53"),sQuery(id+"F2.wireOp",EDGE,"E300.54"),sQuery(id+"F2.wireOp",EDGE,"E300.55"),sQuery(id+"F2.wireOp",EDGE,"E300.56"),sQuery(id+"F2.wireOp",EDGE,"E300.57"),sQuery(id+"F2.wireOp",EDGE,"E300.58"),sQuery(id+"F2.wireOp",EDGE,"E300.59"),sQuery(id+"F2.wireOp",EDGE,"E300.60"),sQuery(id+"F2.wireOp",EDGE,"E300.61"),sQuery(id+"F2.wireOp",EDGE,"E300.62"),sQuery(id+"F2.wireOp",EDGE,"E300.63"),sQuery(id+"F2.wireOp",EDGE,"E300.64"),sQuery(id+"F2.wireOp",EDGE,"E300.65"),sQuery(id+"F2.wireOp",EDGE,"E300.66"),sQuery(id+"F2.wireOp",EDGE,"E300.67"),sQuery(id+"F2.wireOp",EDGE,"E300.68"),sQuery(id+"F2.wireOp",EDGE,"E300.69"),sQuery(id+"F2.wireOp",EDGE,"E300.70"),sQuery(id+"F2.wireOp",EDGE,"E300.71"),sQuery(id+"F2.wireOp",EDGE,"E300.72"),sQuery(id+"F2.wireOp",EDGE,"E300.73"),sQuery(id+"F2.wireOp",EDGE,"E300.74"),sQuery(id+"F2.wireOp",EDGE,"E300.75"),sQuery(id+"F2.wireOp",EDGE,"E300.76"),sQuery(id+"F2.wireOp",EDGE,"E300.77"),sQuery(id+"F2.wireOp",EDGE,"E300.78"),sQuery(id+"F2.wireOp",EDGE,"E300.79"),sQuery(id+"F2.wireOp",EDGE,"E300.80"),sQuery(id+"F2.wireOp",EDGE,"E300.81"),sQuery(id+"F2.wireOp",EDGE,"E300.82"),sQuery(id+"F2.wireOp",EDGE,"E300.83"),sQuery(id+"F2.wireOp",EDGE,"E300.84"),sQuery(id+"F2.wireOp",EDGE,"E300.85"),sQuery(id+"F2.wireOp",EDGE,"E300.86"),sQuery(id+"F2.wireOp",EDGE,"E300.87"),sQuery(id+"F2.wireOp",EDGE,"E300.88"),sQuery(id+"F2.wireOp",EDGE,"E300.89"),sQuery(id+"F2.wireOp",EDGE,"E300.90"),sQuery(id+"F2.wireOp",EDGE,"E300.91"),sQuery(id+"F2.wireOp",EDGE,"E300.92"),sQuery(id+"F2.wireOp",EDGE,"E300.93"),sQuery(id+"F2.wireOp",EDGE,"E300.94"),sQuery(id+"F2.wireOp",EDGE,"E300.95"),sQuery(id+"F2.wireOp",EDGE,"E300.96"),sQuery(id+"F2.wireOp",EDGE,"E300.97"),sQuery(id+"F2.wireOp",EDGE,"E300.98"),sQuery(id+"F2.wireOp",EDGE,"E300.99"),sQuery(id+"F2.wireOp",EDGE,"E300.100"),sQuery(id+"F2.wireOp",EDGE,"E300.101"),sQuery(id+"F2.wireOp",EDGE,"E300.102"),sQuery(id+"F2.wireOp",EDGE,"E300.103"),sQuery(id+"F2.wireOp",EDGE,"E300.104"),sQuery(id+"F2.wireOp",EDGE,"E300.105"),sQuery(id+"F2.wireOp",EDGE,"E300.106"),sQuery(id+"F2.wireOp",EDGE,"E300.107"),sQuery(id+"F2.wireOp",EDGE,"E300.108"),sQuery(id+"F2.wireOp",EDGE,"E300.109"),sQuery(id+"F2.wireOp",EDGE,"E300.110"),sQuery(id+"F2.wireOp",EDGE,"E300.111"),sQuery(id+"F2.wireOp",EDGE,"E300.112"),sQuery(id+"F2.wireOp",EDGE,"E300.113"),sQuery(id+"F2.wireOp",EDGE,"E300.114"),sQuery(id+"F2.wireOp",EDGE,"E300.115"),sQuery(id+"F2.wireOp",EDGE,"E300.116"),sQuery(id+"F2.wireOp",EDGE,"E300.117"),sQuery(id+"F2.wireOp",EDGE,"E300.118"),sQuery(id+"F2.wireOp",EDGE,"E300.119"),sQuery(id+"F2.wireOp",EDGE,"E300.120"),sQuery(id+"F2.wireOp",EDGE,"E300.121"),sQuery(id+"F2.wireOp",EDGE,"E300.122"),sQuery(id+"F2.wireOp",EDGE,"E300.123"),sQuery(id+"F2.wireOp",EDGE,"E300.124"),sQuery(id+"F2.wireOp",EDGE,"E300.125"),sQuery(id+"F2.wireOp",EDGE,"E300.126"),sQuery(id+"F2.wireOp",EDGE,"E300.127"),sQuery(id+"F2.wireOp",EDGE,"E300.128"),sQuery(id+"F2.wireOp",EDGE,"E300.129"),sQuery(id+"F2.wireOp",EDGE,"E300.130"),sQuery(id+"F2.wireOp",EDGE,"E300.131"),sQuery(id+"F2.wireOp",EDGE,"E300.132"),sQuery(id+"F2.wireOp",EDGE,"E300.133"),sQuery(id+"F2.wireOp",EDGE,"E300.134"),sQuery(id+"F2.wireOp",EDGE,"E300.135"),sQuery(id+"F2.wireOp",EDGE,"E300.136"),sQuery(id+"F2.wireOp",EDGE,"E300.137"),sQuery(id+"F2.wireOp",EDGE,"E300.138"),sQuery(id+"F2.wireOp",EDGE,"E300.139"),sQuery(id+"F2.wireOp",EDGE,"E300.140"),sQuery(id+"F2.wireOp",EDGE,"E300.141"),sQuery(id+"F2.wireOp",EDGE,"E300.142"),sQuery(id+"F2.wireOp",EDGE,"E300.143"),sQuery(id+"F2.wireOp",EDGE,"E300.144"),sQuery(id+"F2.wireOp",EDGE,"E300.145"),sQuery(id+"F2.wireOp",EDGE,"E300.146"),sQuery(id+"F2.wireOp",EDGE,"E300.147"),sQuery(id+"F2.wireOp",EDGE,"E300.148"),sQuery(id+"F2.wireOp",EDGE,"E300.149"),sQuery(id+"F2.wireOp",EDGE,"E300.150"),sQuery(id+"F2.wireOp",EDGE,"E300.151"),sQuery(id+"F2.wireOp",EDGE,"E300.152"),sQuery(id+"F2.wireOp",EDGE,"E300.153"),sQuery(id+"F2.wireOp",EDGE,"E300.154"),sQuery(id+"F2.wireOp",EDGE,"E300.155"),sQuery(id+"F2.wireOp",EDGE,"E300.156"),sQuery(id+"F2.wireOp",EDGE,"E300.157"),sQuery(id+"F2.wireOp",EDGE,"E300.158"),sQuery(id+"F2.wireOp",EDGE,"E300.159"),sQuery(id+"F2.wireOp",EDGE,"E300.160")])],"isStart":false});
            shell(context, id + "F5", {"entities" : qUnion([Q0]), "thickness" : 1 * mm});
        }
        {
            var Q0;
            Q0=makeQuery(id+"F1.imprint","IMPRINT",FACE,{"disambiguationData":[TD([[makeQuery(id+"F1.imprint","IMPRINT",EDGE,{"derivedFrom":sQuery(id+"F1.wireOp",EDGE,"E289.0")}),1.0]])]});
            extrude(context, id + "F6", {"entities" : qUnion([Q0]), "operationType" : NewBodyOperationType.REMOVE, "depth" : 59.5 * mm, "offsetDistance" : 25 * mm});
        }
        {
            var Q0;
            Q0=makeQuery(id+"F3.opExtrude","SWEPT_BODY",BODY,{"disambiguationData":[OSD([sQuery(id+"F2.wireOp",EDGE,"E300.0"),sQuery(id+"F2.wireOp",EDGE,"E300.1"),sQuery(id+"F2.wireOp",EDGE,"E300.2"),sQuery(id+"F2.wireOp",EDGE,"E300.3"),sQuery(id+"F2.wireOp",EDGE,"E300.4"),sQuery(id+"F2.wireOp",EDGE,"E300.5"),sQuery(id+"F2.wireOp",EDGE,"E300.6"),sQuery(id+"F2.wireOp",EDGE,"E300.7"),sQuery(id+"F2.wireOp",EDGE,"E300.8"),sQuery(id+"F2.wireOp",EDGE,"E300.9"),sQuery(id+"F2.wireOp",EDGE,"E300.10"),sQuery(id+"F2.wireOp",EDGE,"E300.11"),sQuery(id+"F2.wireOp",EDGE,"E300.12"),sQuery(id+"F2.wireOp",EDGE,"E300.13"),sQuery(id+"F2.wireOp",EDGE,"E300.14"),sQuery(id+"F2.wireOp",EDGE,"E300.15"),sQuery(id+"F2.wireOp",EDGE,"E300.16"),sQuery(id+"F2.wireOp",EDGE,"E300.17"),sQuery(id+"F2.wireOp",EDGE,"E300.18"),sQuery(id+"F2.wireOp",EDGE,"E300.19"),sQuery(id+"F2.wireOp",EDGE,"E300.20"),sQuery(id+"F2.wireOp",EDGE,"E300.21"),sQuery(id+"F2.wireOp",EDGE,"E300.22"),sQuery(id+"F2.wireOp",EDGE,"E300.23"),sQuery(id+"F2.wireOp",EDGE,"E300.24"),sQuery(id+"F2.wireOp",EDGE,"E300.25"),sQuery(id+"F2.wireOp",EDGE,"E300.26"),sQuery(id+"F2.wireOp",EDGE,"E300.27"),sQuery(id+"F2.wireOp",EDGE,"E300.28"),sQuery(id+"F2.wireOp",EDGE,"E300.29"),sQuery(id+"F2.wireOp",EDGE,"E300.30"),sQuery(id+"F2.wireOp",EDGE,"E300.31"),sQuery(id+"F2.wireOp",EDGE,"E300.32"),sQuery(id+"F2.wireOp",EDGE,"E300.33"),sQuery(id+"F2.wireOp",EDGE,"E300.34"),sQuery(id+"F2.wireOp",EDGE,"E300.35"),sQuery(id+"F2.wireOp",EDGE,"E300.36"),sQuery(id+"F2.wireOp",EDGE,"E300.37"),sQuery(id+"F2.wireOp",EDGE,"E300.38"),sQuery(id+"F2.wireOp",EDGE,"E300.39"),sQuery(id+"F2.wireOp",EDGE,"E300.40"),sQuery(id+"F2.wireOp",EDGE,"E300.41"),sQuery(id+"F2.wireOp",EDGE,"E300.42"),sQuery(id+"F2.wireOp",EDGE,"E300.43"),sQuery(id+"F2.wireOp",EDGE,"E300.44"),sQuery(id+"F2.wireOp",EDGE,"E300.45"),sQuery(id+"F2.wireOp",EDGE,"E300.46"),sQuery(id+"F2.wireOp",EDGE,"E300.47"),sQuery(id+"F2.wireOp",EDGE,"E300.48"),sQuery(id+"F2.wireOp",EDGE,"E300.49"),sQuery(id+"F2.wireOp",EDGE,"E300.50"),sQuery(id+"F2.wireOp",EDGE,"E300.51"),sQuery(id+"F2.wireOp",EDGE,"E300.52"),sQuery(id+"F2.wireOp",EDGE,"E300.53"),sQuery(id+"F2.wireOp",EDGE,"E300.54"),sQuery(id+"F2.wireOp",EDGE,"E300.55"),sQuery(id+"F2.wireOp",EDGE,"E300.56"),sQuery(id+"F2.wireOp",EDGE,"E300.57"),sQuery(id+"F2.wireOp",EDGE,"E300.58"),sQuery(id+"F2.wireOp",EDGE,"E300.59"),sQuery(id+"F2.wireOp",EDGE,"E300.60"),sQuery(id+"F2.wireOp",EDGE,"E300.61"),sQuery(id+"F2.wireOp",EDGE,"E300.62"),sQuery(id+"F2.wireOp",EDGE,"E300.63"),sQuery(id+"F2.wireOp",EDGE,"E300.64"),sQuery(id+"F2.wireOp",EDGE,"E300.65"),sQuery(id+"F2.wireOp",EDGE,"E300.66"),sQuery(id+"F2.wireOp",EDGE,"E300.67"),sQuery(id+"F2.wireOp",EDGE,"E300.68"),sQuery(id+"F2.wireOp",EDGE,"E300.69"),sQuery(id+"F2.wireOp",EDGE,"E300.70"),sQuery(id+"F2.wireOp",EDGE,"E300.71"),sQuery(id+"F2.wireOp",EDGE,"E300.72"),sQuery(id+"F2.wireOp",EDGE,"E300.73"),sQuery(id+"F2.wireOp",EDGE,"E300.74"),sQuery(id+"F2.wireOp",EDGE,"E300.75"),sQuery(id+"F2.wireOp",EDGE,"E300.76"),sQuery(id+"F2.wireOp",EDGE,"E300.77"),sQuery(id+"F2.wireOp",EDGE,"E300.78"),sQuery(id+"F2.wireOp",EDGE,"E300.79"),sQuery(id+"F2.wireOp",EDGE,"E300.80"),sQuery(id+"F2.wireOp",EDGE,"E300.81"),sQuery(id+"F2.wireOp",EDGE,"E300.82"),sQuery(id+"F2.wireOp",EDGE,"E300.83"),sQuery(id+"F2.wireOp",EDGE,"E300.84"),sQuery(id+"F2.wireOp",EDGE,"E300.85"),sQuery(id+"F2.wireOp",EDGE,"E300.86"),sQuery(id+"F2.wireOp",EDGE,"E300.87"),sQuery(id+"F2.wireOp",EDGE,"E300.88"),sQuery(id+"F2.wireOp",EDGE,"E300.89"),sQuery(id+"F2.wireOp",EDGE,"E300.90"),sQuery(id+"F2.wireOp",EDGE,"E300.91"),sQuery(id+"F2.wireOp",EDGE,"E300.92"),sQuery(id+"F2.wireOp",EDGE,"E300.93"),sQuery(id+"F2.wireOp",EDGE,"E300.94"),sQuery(id+"F2.wireOp",EDGE,"E300.95"),sQuery(id+"F2.wireOp",EDGE,"E300.96"),sQuery(id+"F2.wireOp",EDGE,"E300.97"),sQuery(id+"F2.wireOp",EDGE,"E300.98"),sQuery(id+"F2.wireOp",EDGE,"E300.99"),sQuery(id+"F2.wireOp",EDGE,"E300.100"),sQuery(id+"F2.wireOp",EDGE,"E300.101"),sQuery(id+"F2.wireOp",EDGE,"E300.102"),sQuery(id+"F2.wireOp",EDGE,"E300.103"),sQuery(id+"F2.wireOp",EDGE,"E300.104"),sQuery(id+"F2.wireOp",EDGE,"E300.105"),sQuery(id+"F2.wireOp",EDGE,"E300.106"),sQuery(id+"F2.wireOp",EDGE,"E300.107"),sQuery(id+"F2.wireOp",EDGE,"E300.108"),sQuery(id+"F2.wireOp",EDGE,"E300.109"),sQuery(id+"F2.wireOp",EDGE,"E300.110"),sQuery(id+"F2.wireOp",EDGE,"E300.111"),sQuery(id+"F2.wireOp",EDGE,"E300.112"),sQuery(id+"F2.wireOp",EDGE,"E300.113"),sQuery(id+"F2.wireOp",EDGE,"E300.114"),sQuery(id+"F2.wireOp",EDGE,"E300.115"),sQuery(id+"F2.wireOp",EDGE,"E300.116"),sQuery(id+"F2.wireOp",EDGE,"E300.117"),sQuery(id+"F2.wireOp",EDGE,"E300.118"),sQuery(id+"F2.wireOp",EDGE,"E300.119"),sQuery(id+"F2.wireOp",EDGE,"E300.120"),sQuery(id+"F2.wireOp",EDGE,"E300.121"),sQuery(id+"F2.wireOp",EDGE,"E300.122"),sQuery(id+"F2.wireOp",EDGE,"E300.123"),sQuery(id+"F2.wireOp",EDGE,"E300.124"),sQuery(id+"F2.wireOp",EDGE,"E300.125"),sQuery(id+"F2.wireOp",EDGE,"E300.126"),sQuery(id+"F2.wireOp",EDGE,"E300.127"),sQuery(id+"F2.wireOp",EDGE,"E300.128"),sQuery(id+"F2.wireOp",EDGE,"E300.129"),sQuery(id+"F2.wireOp",EDGE,"E300.130"),sQuery(id+"F2.wireOp",EDGE,"E300.131"),sQuery(id+"F2.wireOp",EDGE,"E300.132"),sQuery(id+"F2.wireOp",EDGE,"E300.133"),sQuery(id+"F2.wireOp",EDGE,"E300.134"),sQuery(id+"F2.wireOp",EDGE,"E300.135"),sQuery(id+"F2.wireOp",EDGE,"E300.136"),sQuery(id+"F2.wireOp",EDGE,"E300.137"),sQuery(id+"F2.wireOp",EDGE,"E300.138"),sQuery(id+"F2.wireOp",EDGE,"E300.139"),sQuery(id+"F2.wireOp",EDGE,"E300.140"),sQuery(id+"F2.wireOp",EDGE,"E300.141"),sQuery(id+"F2.wireOp",EDGE,"E300.142"),sQuery(id+"F2.wireOp",EDGE,"E300.143"),sQuery(id+"F2.wireOp",EDGE,"E300.144"),sQuery(id+"F2.wireOp",EDGE,"E300.145"),sQuery(id+"F2.wireOp",EDGE,"E300.146"),sQuery(id+"F2.wireOp",EDGE,"E300.147"),sQuery(id+"F2.wireOp",EDGE,"E300.148"),sQuery(id+"F2.wireOp",EDGE,"E300.149"),sQuery(id+"F2.wireOp",EDGE,"E300.150"),sQuery(id+"F2.wireOp",EDGE,"E300.151"),sQuery(id+"F2.wireOp",EDGE,"E300.152"),sQuery(id+"F2.wireOp",EDGE,"E300.153"),sQuery(id+"F2.wireOp",EDGE,"E300.154"),sQuery(id+"F2.wireOp",EDGE,"E300.155"),sQuery(id+"F2.wireOp",EDGE,"E300.156"),sQuery(id+"F2.wireOp",EDGE,"E300.157"),sQuery(id+"F2.wireOp",EDGE,"E300.158"),sQuery(id+"F2.wireOp",EDGE,"E300.159"),sQuery(id+"F2.wireOp",EDGE,"E300.160")])]});
            var Q1;
            Q1=qCreatedBy(id+"F4.planeOp",FACE);
            mirror(context, id + "F7", {"entities" : qUnion([Q0]), "mirrorPlane" : qUnion([Q1])});
        }
        {
            var Q0;
            Q0=makeQuery(id+"F3.opExtrude","SWEPT_BODY",BODY,{"disambiguationData":[OSD([sQuery(id+"F2.wireOp",EDGE,"E300.0"),sQuery(id+"F2.wireOp",EDGE,"E300.1"),sQuery(id+"F2.wireOp",EDGE,"E300.2"),sQuery(id+"F2.wireOp",EDGE,"E300.3"),sQuery(id+"F2.wireOp",EDGE,"E300.4"),sQuery(id+"F2.wireOp",EDGE,"E300.5"),sQuery(id+"F2.wireOp",EDGE,"E300.6"),sQuery(id+"F2.wireOp",EDGE,"E300.7"),sQuery(id+"F2.wireOp",EDGE,"E300.8"),sQuery(id+"F2.wireOp",EDGE,"E300.9"),sQuery(id+"F2.wireOp",EDGE,"E300.10"),sQuery(id+"F2.wireOp",EDGE,"E300.11"),sQuery(id+"F2.wireOp",EDGE,"E300.12"),sQuery(id+"F2.wireOp",EDGE,"E300.13"),sQuery(id+"F2.wireOp",EDGE,"E300.14"),sQuery(id+"F2.wireOp",EDGE,"E300.15"),sQuery(id+"F2.wireOp",EDGE,"E300.16"),sQuery(id+"F2.wireOp",EDGE,"E300.17"),sQuery(id+"F2.wireOp",EDGE,"E300.18"),sQuery(id+"F2.wireOp",EDGE,"E300.19"),sQuery(id+"F2.wireOp",EDGE,"E300.20"),sQuery(id+"F2.wireOp",EDGE,"E300.21"),sQuery(id+"F2.wireOp",EDGE,"E300.22"),sQuery(id+"F2.wireOp",EDGE,"E300.23"),sQuery(id+"F2.wireOp",EDGE,"E300.24"),sQuery(id+"F2.wireOp",EDGE,"E300.25"),sQuery(id+"F2.wireOp",EDGE,"E300.26"),sQuery(id+"F2.wireOp",EDGE,"E300.27"),sQuery(id+"F2.wireOp",EDGE,"E300.28"),sQuery(id+"F2.wireOp",EDGE,"E300.29"),sQuery(id+"F2.wireOp",EDGE,"E300.30"),sQuery(id+"F2.wireOp",EDGE,"E300.31"),sQuery(id+"F2.wireOp",EDGE,"E300.32"),sQuery(id+"F2.wireOp",EDGE,"E300.33"),sQuery(id+"F2.wireOp",EDGE,"E300.34"),sQuery(id+"F2.wireOp",EDGE,"E300.35"),sQuery(id+"F2.wireOp",EDGE,"E300.36"),sQuery(id+"F2.wireOp",EDGE,"E300.37"),sQuery(id+"F2.wireOp",EDGE,"E300.38"),sQuery(id+"F2.wireOp",EDGE,"E300.39"),sQuery(id+"F2.wireOp",EDGE,"E300.40"),sQuery(id+"F2.wireOp",EDGE,"E300.41"),sQuery(id+"F2.wireOp",EDGE,"E300.42"),sQuery(id+"F2.wireOp",EDGE,"E300.43"),sQuery(id+"F2.wireOp",EDGE,"E300.44"),sQuery(id+"F2.wireOp",EDGE,"E300.45"),sQuery(id+"F2.wireOp",EDGE,"E300.46"),sQuery(id+"F2.wireOp",EDGE,"E300.47"),sQuery(id+"F2.wireOp",EDGE,"E300.48"),sQuery(id+"F2.wireOp",EDGE,"E300.49"),sQuery(id+"F2.wireOp",EDGE,"E300.50"),sQuery(id+"F2.wireOp",EDGE,"E300.51"),sQuery(id+"F2.wireOp",EDGE,"E300.52"),sQuery(id+"F2.wireOp",EDGE,"E300.53"),sQuery(id+"F2.wireOp",EDGE,"E300.54"),sQuery(id+"F2.wireOp",EDGE,"E300.55"),sQuery(id+"F2.wireOp",EDGE,"E300.56"),sQuery(id+"F2.wireOp",EDGE,"E300.57"),sQuery(id+"F2.wireOp",EDGE,"E300.58"),sQuery(id+"F2.wireOp",EDGE,"E300.59"),sQuery(id+"F2.wireOp",EDGE,"E300.60"),sQuery(id+"F2.wireOp",EDGE,"E300.61"),sQuery(id+"F2.wireOp",EDGE,"E300.62"),sQuery(id+"F2.wireOp",EDGE,"E300.63"),sQuery(id+"F2.wireOp",EDGE,"E300.64"),sQuery(id+"F2.wireOp",EDGE,"E300.65"),sQuery(id+"F2.wireOp",EDGE,"E300.66"),sQuery(id+"F2.wireOp",EDGE,"E300.67"),sQuery(id+"F2.wireOp",EDGE,"E300.68"),sQuery(id+"F2.wireOp",EDGE,"E300.69"),sQuery(id+"F2.wireOp",EDGE,"E300.70"),sQuery(id+"F2.wireOp",EDGE,"E300.71"),sQuery(id+"F2.wireOp",EDGE,"E300.72"),sQuery(id+"F2.wireOp",EDGE,"E300.73"),sQuery(id+"F2.wireOp",EDGE,"E300.74"),sQuery(id+"F2.wireOp",EDGE,"E300.75"),sQuery(id+"F2.wireOp",EDGE,"E300.76"),sQuery(id+"F2.wireOp",EDGE,"E300.77"),sQuery(id+"F2.wireOp",EDGE,"E300.78"),sQuery(id+"F2.wireOp",EDGE,"E300.79"),sQuery(id+"F2.wireOp",EDGE,"E300.80"),sQuery(id+"F2.wireOp",EDGE,"E300.81"),sQuery(id+"F2.wireOp",EDGE,"E300.82"),sQuery(id+"F2.wireOp",EDGE,"E300.83"),sQuery(id+"F2.wireOp",EDGE,"E300.84"),sQuery(id+"F2.wireOp",EDGE,"E300.85"),sQuery(id+"F2.wireOp",EDGE,"E300.86"),sQuery(id+"F2.wireOp",EDGE,"E300.87"),sQuery(id+"F2.wireOp",EDGE,"E300.88"),sQuery(id+"F2.wireOp",EDGE,"E300.89"),sQuery(id+"F2.wireOp",EDGE,"E300.90"),sQuery(id+"F2.wireOp",EDGE,"E300.91"),sQuery(id+"F2.wireOp",EDGE,"E300.92"),sQuery(id+"F2.wireOp",EDGE,"E300.93"),sQuery(id+"F2.wireOp",EDGE,"E300.94"),sQuery(id+"F2.wireOp",EDGE,"E300.95"),sQuery(id+"F2.wireOp",EDGE,"E300.96"),sQuery(id+"F2.wireOp",EDGE,"E300.97"),sQuery(id+"F2.wireOp",EDGE,"E300.98"),sQuery(id+"F2.wireOp",EDGE,"E300.99"),sQuery(id+"F2.wireOp",EDGE,"E300.100"),sQuery(id+"F2.wireOp",EDGE,"E300.101"),sQuery(id+"F2.wireOp",EDGE,"E300.102"),sQuery(id+"F2.wireOp",EDGE,"E300.103"),sQuery(id+"F2.wireOp",EDGE,"E300.104"),sQuery(id+"F2.wireOp",EDGE,"E300.105"),sQuery(id+"F2.wireOp",EDGE,"E300.106"),sQuery(id+"F2.wireOp",EDGE,"E300.107"),sQuery(id+"F2.wireOp",EDGE,"E300.108"),sQuery(id+"F2.wireOp",EDGE,"E300.109"),sQuery(id+"F2.wireOp",EDGE,"E300.110"),sQuery(id+"F2.wireOp",EDGE,"E300.111"),sQuery(id+"F2.wireOp",EDGE,"E300.112"),sQuery(id+"F2.wireOp",EDGE,"E300.113"),sQuery(id+"F2.wireOp",EDGE,"E300.114"),sQuery(id+"F2.wireOp",EDGE,"E300.115"),sQuery(id+"F2.wireOp",EDGE,"E300.116"),sQuery(id+"F2.wireOp",EDGE,"E300.117"),sQuery(id+"F2.wireOp",EDGE,"E300.118"),sQuery(id+"F2.wireOp",EDGE,"E300.119"),sQuery(id+"F2.wireOp",EDGE,"E300.120"),sQuery(id+"F2.wireOp",EDGE,"E300.121"),sQuery(id+"F2.wireOp",EDGE,"E300.122"),sQuery(id+"F2.wireOp",EDGE,"E300.123"),sQuery(id+"F2.wireOp",EDGE,"E300.124"),sQuery(id+"F2.wireOp",EDGE,"E300.125"),sQuery(id+"F2.wireOp",EDGE,"E300.126"),sQuery(id+"F2.wireOp",EDGE,"E300.127"),sQuery(id+"F2.wireOp",EDGE,"E300.128"),sQuery(id+"F2.wireOp",EDGE,"E300.129"),sQuery(id+"F2.wireOp",EDGE,"E300.130"),sQuery(id+"F2.wireOp",EDGE,"E300.131"),sQuery(id+"F2.wireOp",EDGE,"E300.132"),sQuery(id+"F2.wireOp",EDGE,"E300.133"),sQuery(id+"F2.wireOp",EDGE,"E300.134"),sQuery(id+"F2.wireOp",EDGE,"E300.135"),sQuery(id+"F2.wireOp",EDGE,"E300.136"),sQuery(id+"F2.wireOp",EDGE,"E300.137"),sQuery(id+"F2.wireOp",EDGE,"E300.138"),sQuery(id+"F2.wireOp",EDGE,"E300.139"),sQuery(id+"F2.wireOp",EDGE,"E300.140"),sQuery(id+"F2.wireOp",EDGE,"E300.141"),sQuery(id+"F2.wireOp",EDGE,"E300.142"),sQuery(id+"F2.wireOp",EDGE,"E300.143"),sQuery(id+"F2.wireOp",EDGE,"E300.144"),sQuery(id+"F2.wireOp",EDGE,"E300.145"),sQuery(id+"F2.wireOp",EDGE,"E300.146"),sQuery(id+"F2.wireOp",EDGE,"E300.147"),sQuery(id+"F2.wireOp",EDGE,"E300.148"),sQuery(id+"F2.wireOp",EDGE,"E300.149"),sQuery(id+"F2.wireOp",EDGE,"E300.150"),sQuery(id+"F2.wireOp",EDGE,"E300.151"),sQuery(id+"F2.wireOp",EDGE,"E300.152"),sQuery(id+"F2.wireOp",EDGE,"E300.153"),sQuery(id+"F2.wireOp",EDGE,"E300.154"),sQuery(id+"F2.wireOp",EDGE,"E300.155"),sQuery(id+"F2.wireOp",EDGE,"E300.156"),sQuery(id+"F2.wireOp",EDGE,"E300.157"),sQuery(id+"F2.wireOp",EDGE,"E300.158"),sQuery(id+"F2.wireOp",EDGE,"E300.159"),sQuery(id+"F2.wireOp",EDGE,"E300.160")])]});
            transform(context, id + "F8", {"entities" : qUnion([Q0]), "transformType" : TransformType.COPY});
        }
    });
